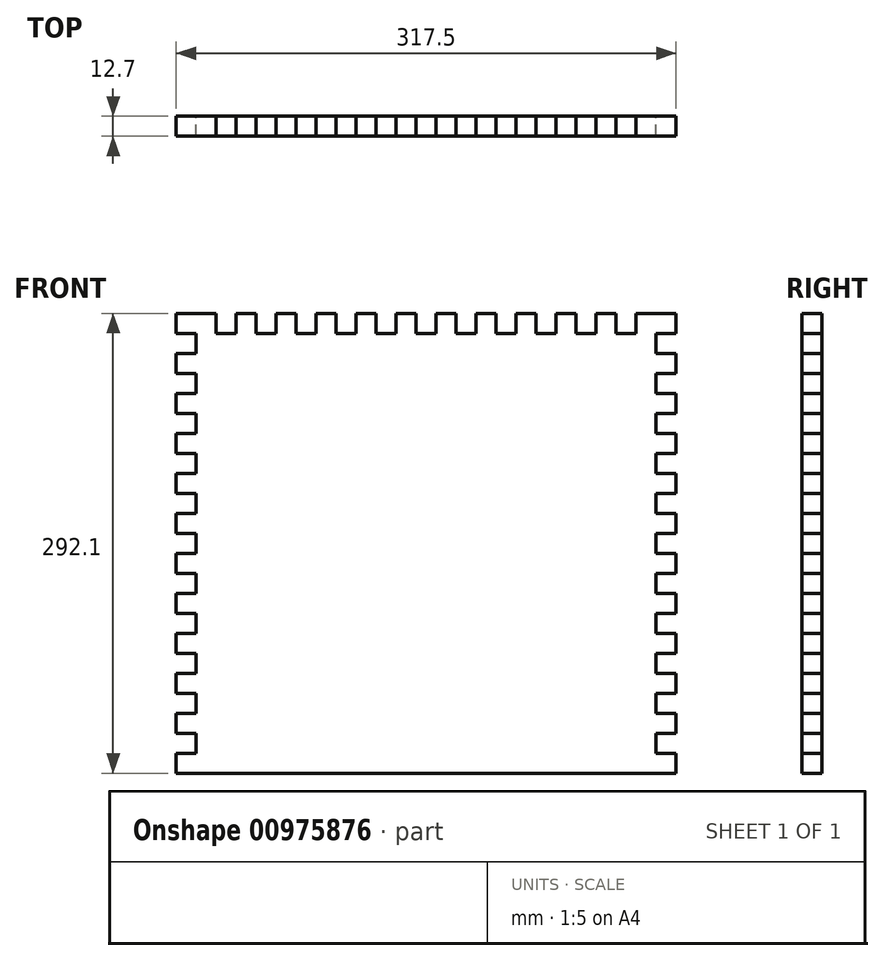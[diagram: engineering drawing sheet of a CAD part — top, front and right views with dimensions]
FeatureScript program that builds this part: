
annotation { "Feature Type Name" : "Feature", "Feature Type Description" : "" }
export const myFeature = defineFeature(function(context is Context, id is Id, definition is map)
    precondition{}
    {
        {
            var Q0;
            Q0=qCreatedBy(makeId("Front.planeOp"),FACE);
            var sketch = newSketch(context, id + "F0", { "sketchPlane" : qUnion([Q0])});
            skLineSegment(sketch, "E0.bottom", {"start": v(-125, 189.2) * mm, "end": v(167.1, 189.2) * mm});
            skLineSegment(sketch, "E0.top", {"start": v(-125, -102.9) * mm, "end": v(167.1, -102.9) * mm});
            skLineSegment(sketch, "E0.left", {"start": v(-125, 189.2) * mm, "end": v(-125, -102.9) * mm});
            skLineSegment(sketch, "E0.right", {"start": v(167.1, 189.2) * mm, "end": v(167.1, -102.9) * mm});
            skLineSegment(sketch, "E1.bottom", {"start": v(-125, 189.2) * mm, "end": v(-137.7, 189.2) * mm});
            skLineSegment(sketch, "E1.top", {"start": v(-125, 176.5) * mm, "end": v(-137.7, 176.5) * mm});
            skLineSegment(sketch, "E1.left", {"start": v(-125, 189.2) * mm, "end": v(-125, 176.5) * mm});
            skLineSegment(sketch, "E1.right", {"start": v(-137.7, 189.2) * mm, "end": v(-137.7, 176.5) * mm});
            skLineSegment(sketch, "E2.bottom", {"start": v(167.1, 189.2) * mm, "end": v(179.8, 189.2) * mm});
            skLineSegment(sketch, "E2.top", {"start": v(167.1, 176.5) * mm, "end": v(179.8, 176.5) * mm});
            skLineSegment(sketch, "E2.left", {"start": v(167.1, 189.2) * mm, "end": v(167.1, 176.5) * mm});
            skLineSegment(sketch, "E2.right", {"start": v(179.8, 189.2) * mm, "end": v(179.8, 176.5) * mm});
            skLineSegment(sketch, "E3.direction2", {"start": v(167.1, 176.5) * mm, "end": v(167.1, 176.5) * mm});
            skLineSegment(sketch, "E4.bottom", {"start": v(-112.3, 189.2) * mm, "end": v(-99.6, 189.2) * mm});
            skLineSegment(sketch, "E4.top", {"start": v(-112.3, 176.5) * mm, "end": v(-99.6, 176.5) * mm});
            skLineSegment(sketch, "E4.left", {"start": v(-112.3, 189.2) * mm, "end": v(-112.3, 176.5) * mm});
            skLineSegment(sketch, "E4.right", {"start": v(-99.6, 189.2) * mm, "end": v(-99.6, 176.5) * mm});
            skLineSegment(sketch, "E5.1.0.0", {"start": v(-86.9, 189.2) * mm, "end": v(-74.2, 189.2) * mm});
            skLineSegment(sketch, "E5.1.0.1", {"start": v(-86.9, 176.5) * mm, "end": v(-74.2, 176.5) * mm});
            skLineSegment(sketch, "E5.1.0.2", {"start": v(-74.2, 189.2) * mm, "end": v(-74.2, 176.5) * mm});
            skLineSegment(sketch, "E5.1.0.3", {"start": v(-86.9, 189.2) * mm, "end": v(-86.9, 176.5) * mm});
            skLineSegment(sketch, "E5.2.0.0", {"start": v(-61.5, 189.2) * mm, "end": v(-48.8, 189.2) * mm});
            skLineSegment(sketch, "E5.2.0.1", {"start": v(-61.5, 176.5) * mm, "end": v(-48.8, 176.5) * mm});
            skLineSegment(sketch, "E5.2.0.2", {"start": v(-48.8, 189.2) * mm, "end": v(-48.8, 176.5) * mm});
            skLineSegment(sketch, "E5.2.0.3", {"start": v(-61.5, 189.2) * mm, "end": v(-61.5, 176.5) * mm});
            skLineSegment(sketch, "E5.3.0.0", {"start": v(-36.1, 189.2) * mm, "end": v(-23.4, 189.2) * mm});
            skLineSegment(sketch, "E5.3.0.1", {"start": v(-36.1, 176.5) * mm, "end": v(-23.4, 176.5) * mm});
            skLineSegment(sketch, "E5.3.0.2", {"start": v(-23.4, 189.2) * mm, "end": v(-23.4, 176.5) * mm});
            skLineSegment(sketch, "E5.3.0.3", {"start": v(-36.1, 189.2) * mm, "end": v(-36.1, 176.5) * mm});
            skLineSegment(sketch, "E5.4.0.0", {"start": v(-10.7, 189.2) * mm, "end": v(2, 189.2) * mm});
            skLineSegment(sketch, "E5.4.0.1", {"start": v(-10.7, 176.5) * mm, "end": v(2, 176.5) * mm});
            skLineSegment(sketch, "E5.4.0.2", {"start": v(2, 189.2) * mm, "end": v(2, 176.5) * mm});
            skLineSegment(sketch, "E5.4.0.3", {"start": v(-10.7, 189.2) * mm, "end": v(-10.7, 176.5) * mm});
            skLineSegment(sketch, "E5.5.0.0", {"start": v(14.7, 189.2) * mm, "end": v(27.4, 189.2) * mm});
            skLineSegment(sketch, "E5.5.0.1", {"start": v(14.7, 176.5) * mm, "end": v(27.4, 176.5) * mm});
            skLineSegment(sketch, "E5.5.0.2", {"start": v(27.4, 189.2) * mm, "end": v(27.4, 176.5) * mm});
            skLineSegment(sketch, "E5.5.0.3", {"start": v(14.7, 189.2) * mm, "end": v(14.7, 176.5) * mm});
            skLineSegment(sketch, "E5.6.0.0", {"start": v(40.1, 189.2) * mm, "end": v(52.8, 189.2) * mm});
            skLineSegment(sketch, "E5.6.0.1", {"start": v(40.1, 176.5) * mm, "end": v(52.8, 176.5) * mm});
            skLineSegment(sketch, "E5.6.0.2", {"start": v(52.8, 189.2) * mm, "end": v(52.8, 176.5) * mm});
            skLineSegment(sketch, "E5.6.0.3", {"start": v(40.1, 189.2) * mm, "end": v(40.1, 176.5) * mm});
            skLineSegment(sketch, "E5.7.0.0", {"start": v(65.5, 189.2) * mm, "end": v(78.2, 189.2) * mm});
            skLineSegment(sketch, "E5.7.0.1", {"start": v(65.5, 176.5) * mm, "end": v(78.2, 176.5) * mm});
            skLineSegment(sketch, "E5.7.0.2", {"start": v(78.2, 189.2) * mm, "end": v(78.2, 176.5) * mm});
            skLineSegment(sketch, "E5.7.0.3", {"start": v(65.5, 189.2) * mm, "end": v(65.5, 176.5) * mm});
            skLineSegment(sketch, "E5.8.0.0", {"start": v(90.9, 189.2) * mm, "end": v(103.6, 189.2) * mm});
            skLineSegment(sketch, "E5.8.0.1", {"start": v(90.9, 176.5) * mm, "end": v(103.6, 176.5) * mm});
            skLineSegment(sketch, "E5.8.0.2", {"start": v(103.6, 189.2) * mm, "end": v(103.6, 176.5) * mm});
            skLineSegment(sketch, "E5.8.0.3", {"start": v(90.9, 189.2) * mm, "end": v(90.9, 176.5) * mm});
            skLineSegment(sketch, "E5.direction1", {"start": v(-112.3, 176.5) * mm, "end": v(-86.9, 176.5) * mm, "construction": true});
            skLineSegment(sketch, "E6.0.9.0", {"start": v(116.3, 189.2) * mm, "end": v(129, 189.2) * mm});
            skLineSegment(sketch, "E6.3.9.0", {"start": v(116.3, 176.5) * mm, "end": v(129, 176.5) * mm});
            skLineSegment(sketch, "E6.6.9.0", {"start": v(129, 189.2) * mm, "end": v(129, 176.5) * mm});
            skLineSegment(sketch, "E6.9.9.0", {"start": v(116.3, 189.2) * mm, "end": v(116.3, 176.5) * mm});
            skLineSegment(sketch, "E7.0.10.0", {"start": v(141.7, 189.2) * mm, "end": v(154.4, 189.2) * mm});
            skLineSegment(sketch, "E7.3.10.0", {"start": v(141.7, 176.5) * mm, "end": v(154.4, 176.5) * mm});
            skLineSegment(sketch, "E7.6.10.0", {"start": v(154.4, 189.2) * mm, "end": v(154.4, 176.5) * mm});
            skLineSegment(sketch, "E7.9.10.0", {"start": v(141.7, 189.2) * mm, "end": v(141.7, 176.5) * mm});
            skLineSegment(sketch, "E8.0.1.0", {"start": v(167.1, 151.1) * mm, "end": v(179.8, 151.1) * mm});
            skLineSegment(sketch, "E8.0.1.1", {"start": v(179.8, 163.8) * mm, "end": v(179.8, 151.1) * mm});
            skLineSegment(sketch, "E8.0.1.2", {"start": v(167.1, 163.8) * mm, "end": v(167.1, 151.1) * mm});
            skLineSegment(sketch, "E8.0.1.3", {"start": v(167.1, 163.8) * mm, "end": v(179.8, 163.8) * mm});
            skLineSegment(sketch, "E8.0.1.4", {"start": v(167.1, 163.8) * mm, "end": v(167.1, 151.1) * mm});
            skLineSegment(sketch, "E8.0.1.5", {"start": v(167.1, 151.1) * mm, "end": v(179.8, 151.1) * mm});
            skLineSegment(sketch, "E8.0.1.6", {"start": v(179.8, 163.8) * mm, "end": v(179.8, 151.1) * mm});
            skLineSegment(sketch, "E8.0.1.7", {"start": v(167.1, 163.8) * mm, "end": v(179.8, 163.8) * mm});
            skLineSegment(sketch, "E8.0.1.8", {"start": v(167.1, 163.8) * mm, "end": v(167.1, 151.1) * mm});
            skLineSegment(sketch, "E8.0.1.9", {"start": v(167.1, 151.1) * mm, "end": v(179.8, 151.1) * mm});
            skLineSegment(sketch, "E8.0.1.10", {"start": v(179.8, 163.8) * mm, "end": v(179.8, 151.1) * mm});
            skLineSegment(sketch, "E8.0.1.11", {"start": v(167.1, 163.8) * mm, "end": v(179.8, 163.8) * mm});
            skLineSegment(sketch, "E8.0.1.12", {"start": v(167.1, 151.1) * mm, "end": v(179.8, 151.1) * mm});
            skLineSegment(sketch, "E8.0.1.13", {"start": v(179.8, 163.8) * mm, "end": v(179.8, 151.1) * mm});
            skLineSegment(sketch, "E8.0.1.14", {"start": v(167.1, 163.8) * mm, "end": v(179.8, 163.8) * mm});
            skLineSegment(sketch, "E8.0.1.15", {"start": v(167.1, 163.8) * mm, "end": v(167.1, 151.1) * mm});
            skLineSegment(sketch, "E8.0.1.16", {"start": v(179.8, 163.8) * mm, "end": v(179.8, 151.1) * mm});
            skLineSegment(sketch, "E8.0.1.17", {"start": v(167.1, 163.8) * mm, "end": v(167.1, 151.1) * mm});
            skLineSegment(sketch, "E8.0.1.18", {"start": v(167.1, 163.8) * mm, "end": v(179.8, 163.8) * mm});
            skLineSegment(sketch, "E8.0.1.19", {"start": v(167.1, 151.1) * mm, "end": v(179.8, 151.1) * mm});
            skLineSegment(sketch, "E8.0.1.20", {"start": v(167.1, 163.8) * mm, "end": v(179.8, 163.8) * mm});
            skLineSegment(sketch, "E8.0.1.21", {"start": v(167.1, 151.1) * mm, "end": v(179.8, 151.1) * mm});
            skLineSegment(sketch, "E8.0.1.22", {"start": v(167.1, 163.8) * mm, "end": v(167.1, 151.1) * mm});
            skLineSegment(sketch, "E8.0.1.23", {"start": v(179.8, 163.8) * mm, "end": v(179.8, 151.1) * mm});
            skLineSegment(sketch, "E8.0.1.24", {"start": v(167.1, 163.8) * mm, "end": v(179.8, 163.8) * mm});
            skLineSegment(sketch, "E8.0.1.25", {"start": v(167.1, 163.8) * mm, "end": v(167.1, 151.1) * mm});
            skLineSegment(sketch, "E8.0.1.26", {"start": v(167.1, 151.1) * mm, "end": v(179.8, 151.1) * mm});
            skLineSegment(sketch, "E8.0.1.27", {"start": v(179.8, 163.8) * mm, "end": v(179.8, 151.1) * mm});
            skLineSegment(sketch, "E8.0.1.28", {"start": v(167.1, 163.8) * mm, "end": v(167.1, 151.1) * mm});
            skLineSegment(sketch, "E8.0.1.29", {"start": v(179.8, 163.8) * mm, "end": v(179.8, 151.1) * mm});
            skLineSegment(sketch, "E8.0.1.30", {"start": v(167.1, 163.8) * mm, "end": v(179.8, 163.8) * mm});
            skLineSegment(sketch, "E8.0.1.31", {"start": v(167.1, 151.1) * mm, "end": v(179.8, 151.1) * mm});
            skLineSegment(sketch, "E8.0.1.32", {"start": v(167.1, 163.8) * mm, "end": v(167.1, 151.1) * mm});
            skLineSegment(sketch, "E8.0.1.33", {"start": v(167.1, 163.8) * mm, "end": v(179.8, 163.8) * mm});
            skLineSegment(sketch, "E8.0.1.34", {"start": v(167.1, 151.1) * mm, "end": v(179.8, 151.1) * mm});
            skLineSegment(sketch, "E8.0.1.35", {"start": v(179.8, 163.8) * mm, "end": v(179.8, 151.1) * mm});
            skLineSegment(sketch, "E8.0.1.36", {"start": v(167.1, 151.1) * mm, "end": v(179.8, 151.1) * mm});
            skLineSegment(sketch, "E8.0.1.37", {"start": v(179.8, 163.8) * mm, "end": v(179.8, 151.1) * mm});
            skLineSegment(sketch, "E8.0.1.38", {"start": v(167.1, 163.8) * mm, "end": v(167.1, 151.1) * mm});
            skLineSegment(sketch, "E8.0.1.39", {"start": v(167.1, 163.8) * mm, "end": v(179.8, 163.8) * mm});
            skLineSegment(sketch, "E8.0.1.40", {"start": v(167.1, 163.8) * mm, "end": v(167.1, 151.1) * mm});
            skLineSegment(sketch, "E8.0.1.41", {"start": v(167.1, 151.1) * mm, "end": v(179.8, 151.1) * mm});
            skLineSegment(sketch, "E8.0.1.42", {"start": v(167.1, 163.8) * mm, "end": v(179.8, 163.8) * mm});
            skLineSegment(sketch, "E8.0.1.43", {"start": v(179.8, 163.8) * mm, "end": v(179.8, 151.1) * mm});
            skLineSegment(sketch, "E8.0.1.44", {"start": v(167.1, 163.8) * mm, "end": v(167.1, 151.1) * mm});
            skLineSegment(sketch, "E8.0.1.45", {"start": v(167.1, 151.1) * mm, "end": v(179.8, 151.1) * mm});
            skLineSegment(sketch, "E8.0.1.46", {"start": v(167.1, 163.8) * mm, "end": v(179.8, 163.8) * mm});
            skLineSegment(sketch, "E8.0.1.47", {"start": v(179.8, 163.8) * mm, "end": v(179.8, 151.1) * mm});
            skLineSegment(sketch, "E8.0.2.0", {"start": v(167.1, 125.7) * mm, "end": v(179.8, 125.7) * mm});
            skLineSegment(sketch, "E8.0.2.1", {"start": v(179.8, 138.4) * mm, "end": v(179.8, 125.7) * mm});
            skLineSegment(sketch, "E8.0.2.2", {"start": v(167.1, 138.4) * mm, "end": v(167.1, 125.7) * mm});
            skLineSegment(sketch, "E8.0.2.3", {"start": v(167.1, 138.4) * mm, "end": v(179.8, 138.4) * mm});
            skLineSegment(sketch, "E8.0.2.4", {"start": v(167.1, 138.4) * mm, "end": v(167.1, 125.7) * mm});
            skLineSegment(sketch, "E8.0.2.5", {"start": v(167.1, 125.7) * mm, "end": v(179.8, 125.7) * mm});
            skLineSegment(sketch, "E8.0.2.6", {"start": v(179.8, 138.4) * mm, "end": v(179.8, 125.7) * mm});
            skLineSegment(sketch, "E8.0.2.7", {"start": v(167.1, 138.4) * mm, "end": v(179.8, 138.4) * mm});
            skLineSegment(sketch, "E8.0.2.8", {"start": v(167.1, 138.4) * mm, "end": v(167.1, 125.7) * mm});
            skLineSegment(sketch, "E8.0.2.9", {"start": v(167.1, 125.7) * mm, "end": v(179.8, 125.7) * mm});
            skLineSegment(sketch, "E8.0.2.10", {"start": v(179.8, 138.4) * mm, "end": v(179.8, 125.7) * mm});
            skLineSegment(sketch, "E8.0.2.11", {"start": v(167.1, 138.4) * mm, "end": v(179.8, 138.4) * mm});
            skLineSegment(sketch, "E8.0.2.12", {"start": v(167.1, 125.7) * mm, "end": v(179.8, 125.7) * mm});
            skLineSegment(sketch, "E8.0.2.13", {"start": v(179.8, 138.4) * mm, "end": v(179.8, 125.7) * mm});
            skLineSegment(sketch, "E8.0.2.14", {"start": v(167.1, 138.4) * mm, "end": v(179.8, 138.4) * mm});
            skLineSegment(sketch, "E8.0.2.15", {"start": v(167.1, 138.4) * mm, "end": v(167.1, 125.7) * mm});
            skLineSegment(sketch, "E8.0.2.16", {"start": v(179.8, 138.4) * mm, "end": v(179.8, 125.7) * mm});
            skLineSegment(sketch, "E8.0.2.17", {"start": v(167.1, 138.4) * mm, "end": v(167.1, 125.7) * mm});
            skLineSegment(sketch, "E8.0.2.18", {"start": v(167.1, 138.4) * mm, "end": v(179.8, 138.4) * mm});
            skLineSegment(sketch, "E8.0.2.19", {"start": v(167.1, 125.7) * mm, "end": v(179.8, 125.7) * mm});
            skLineSegment(sketch, "E8.0.2.20", {"start": v(167.1, 138.4) * mm, "end": v(179.8, 138.4) * mm});
            skLineSegment(sketch, "E8.0.2.21", {"start": v(167.1, 125.7) * mm, "end": v(179.8, 125.7) * mm});
            skLineSegment(sketch, "E8.0.2.22", {"start": v(167.1, 138.4) * mm, "end": v(167.1, 125.7) * mm});
            skLineSegment(sketch, "E8.0.2.23", {"start": v(179.8, 138.4) * mm, "end": v(179.8, 125.7) * mm});
            skLineSegment(sketch, "E8.0.2.24", {"start": v(167.1, 138.4) * mm, "end": v(179.8, 138.4) * mm});
            skLineSegment(sketch, "E8.0.2.25", {"start": v(167.1, 138.4) * mm, "end": v(167.1, 125.7) * mm});
            skLineSegment(sketch, "E8.0.2.26", {"start": v(167.1, 125.7) * mm, "end": v(179.8, 125.7) * mm});
            skLineSegment(sketch, "E8.0.2.27", {"start": v(179.8, 138.4) * mm, "end": v(179.8, 125.7) * mm});
            skLineSegment(sketch, "E8.0.2.28", {"start": v(167.1, 138.4) * mm, "end": v(167.1, 125.7) * mm});
            skLineSegment(sketch, "E8.0.2.29", {"start": v(179.8, 138.4) * mm, "end": v(179.8, 125.7) * mm});
            skLineSegment(sketch, "E8.0.2.30", {"start": v(167.1, 138.4) * mm, "end": v(179.8, 138.4) * mm});
            skLineSegment(sketch, "E8.0.2.31", {"start": v(167.1, 125.7) * mm, "end": v(179.8, 125.7) * mm});
            skLineSegment(sketch, "E8.0.2.32", {"start": v(167.1, 138.4) * mm, "end": v(167.1, 125.7) * mm});
            skLineSegment(sketch, "E8.0.2.33", {"start": v(167.1, 138.4) * mm, "end": v(179.8, 138.4) * mm});
            skLineSegment(sketch, "E8.0.2.34", {"start": v(167.1, 125.7) * mm, "end": v(179.8, 125.7) * mm});
            skLineSegment(sketch, "E8.0.2.35", {"start": v(179.8, 138.4) * mm, "end": v(179.8, 125.7) * mm});
            skLineSegment(sketch, "E8.0.2.36", {"start": v(167.1, 125.7) * mm, "end": v(179.8, 125.7) * mm});
            skLineSegment(sketch, "E8.0.2.37", {"start": v(179.8, 138.4) * mm, "end": v(179.8, 125.7) * mm});
            skLineSegment(sketch, "E8.0.2.38", {"start": v(167.1, 138.4) * mm, "end": v(167.1, 125.7) * mm});
            skLineSegment(sketch, "E8.0.2.39", {"start": v(167.1, 138.4) * mm, "end": v(179.8, 138.4) * mm});
            skLineSegment(sketch, "E8.0.2.40", {"start": v(167.1, 138.4) * mm, "end": v(167.1, 125.7) * mm});
            skLineSegment(sketch, "E8.0.2.41", {"start": v(167.1, 125.7) * mm, "end": v(179.8, 125.7) * mm});
            skLineSegment(sketch, "E8.0.2.42", {"start": v(167.1, 138.4) * mm, "end": v(179.8, 138.4) * mm});
            skLineSegment(sketch, "E8.0.2.43", {"start": v(179.8, 138.4) * mm, "end": v(179.8, 125.7) * mm});
            skLineSegment(sketch, "E8.0.2.44", {"start": v(167.1, 138.4) * mm, "end": v(167.1, 125.7) * mm});
            skLineSegment(sketch, "E8.0.2.45", {"start": v(167.1, 125.7) * mm, "end": v(179.8, 125.7) * mm});
            skLineSegment(sketch, "E8.0.2.46", {"start": v(167.1, 138.4) * mm, "end": v(179.8, 138.4) * mm});
            skLineSegment(sketch, "E8.0.2.47", {"start": v(179.8, 138.4) * mm, "end": v(179.8, 125.7) * mm});
            skLineSegment(sketch, "E8.0.3.0", {"start": v(167.1, 100.3) * mm, "end": v(179.8, 100.3) * mm});
            skLineSegment(sketch, "E8.0.3.1", {"start": v(179.8, 113) * mm, "end": v(179.8, 100.3) * mm});
            skLineSegment(sketch, "E8.0.3.2", {"start": v(167.1, 113) * mm, "end": v(167.1, 100.3) * mm});
            skLineSegment(sketch, "E8.0.3.3", {"start": v(167.1, 113) * mm, "end": v(179.8, 113) * mm});
            skLineSegment(sketch, "E8.0.3.4", {"start": v(167.1, 113) * mm, "end": v(167.1, 100.3) * mm});
            skLineSegment(sketch, "E8.0.3.5", {"start": v(167.1, 100.3) * mm, "end": v(179.8, 100.3) * mm});
            skLineSegment(sketch, "E8.0.3.6", {"start": v(179.8, 113) * mm, "end": v(179.8, 100.3) * mm});
            skLineSegment(sketch, "E8.0.3.7", {"start": v(167.1, 113) * mm, "end": v(179.8, 113) * mm});
            skLineSegment(sketch, "E8.0.3.8", {"start": v(167.1, 113) * mm, "end": v(167.1, 100.3) * mm});
            skLineSegment(sketch, "E8.0.3.9", {"start": v(167.1, 100.3) * mm, "end": v(179.8, 100.3) * mm});
            skLineSegment(sketch, "E8.0.3.10", {"start": v(179.8, 113) * mm, "end": v(179.8, 100.3) * mm});
            skLineSegment(sketch, "E8.0.3.11", {"start": v(167.1, 113) * mm, "end": v(179.8, 113) * mm});
            skLineSegment(sketch, "E8.0.3.12", {"start": v(167.1, 100.3) * mm, "end": v(179.8, 100.3) * mm});
            skLineSegment(sketch, "E8.0.3.13", {"start": v(179.8, 113) * mm, "end": v(179.8, 100.3) * mm});
            skLineSegment(sketch, "E8.0.3.14", {"start": v(167.1, 113) * mm, "end": v(179.8, 113) * mm});
            skLineSegment(sketch, "E8.0.3.15", {"start": v(167.1, 113) * mm, "end": v(167.1, 100.3) * mm});
            skLineSegment(sketch, "E8.0.3.16", {"start": v(179.8, 113) * mm, "end": v(179.8, 100.3) * mm});
            skLineSegment(sketch, "E8.0.3.17", {"start": v(167.1, 113) * mm, "end": v(167.1, 100.3) * mm});
            skLineSegment(sketch, "E8.0.3.18", {"start": v(167.1, 113) * mm, "end": v(179.8, 113) * mm});
            skLineSegment(sketch, "E8.0.3.19", {"start": v(167.1, 100.3) * mm, "end": v(179.8, 100.3) * mm});
            skLineSegment(sketch, "E8.0.3.20", {"start": v(167.1, 113) * mm, "end": v(179.8, 113) * mm});
            skLineSegment(sketch, "E8.0.3.21", {"start": v(167.1, 100.3) * mm, "end": v(179.8, 100.3) * mm});
            skLineSegment(sketch, "E8.0.3.22", {"start": v(167.1, 113) * mm, "end": v(167.1, 100.3) * mm});
            skLineSegment(sketch, "E8.0.3.23", {"start": v(179.8, 113) * mm, "end": v(179.8, 100.3) * mm});
            skLineSegment(sketch, "E8.0.3.24", {"start": v(167.1, 113) * mm, "end": v(179.8, 113) * mm});
            skLineSegment(sketch, "E8.0.3.25", {"start": v(167.1, 113) * mm, "end": v(167.1, 100.3) * mm});
            skLineSegment(sketch, "E8.0.3.26", {"start": v(167.1, 100.3) * mm, "end": v(179.8, 100.3) * mm});
            skLineSegment(sketch, "E8.0.3.27", {"start": v(179.8, 113) * mm, "end": v(179.8, 100.3) * mm});
            skLineSegment(sketch, "E8.0.3.28", {"start": v(167.1, 113) * mm, "end": v(167.1, 100.3) * mm});
            skLineSegment(sketch, "E8.0.3.29", {"start": v(179.8, 113) * mm, "end": v(179.8, 100.3) * mm});
            skLineSegment(sketch, "E8.0.3.30", {"start": v(167.1, 113) * mm, "end": v(179.8, 113) * mm});
            skLineSegment(sketch, "E8.0.3.31", {"start": v(167.1, 100.3) * mm, "end": v(179.8, 100.3) * mm});
            skLineSegment(sketch, "E8.0.3.32", {"start": v(167.1, 113) * mm, "end": v(167.1, 100.3) * mm});
            skLineSegment(sketch, "E8.0.3.33", {"start": v(167.1, 113) * mm, "end": v(179.8, 113) * mm});
            skLineSegment(sketch, "E8.0.3.34", {"start": v(167.1, 100.3) * mm, "end": v(179.8, 100.3) * mm});
            skLineSegment(sketch, "E8.0.3.35", {"start": v(179.8, 113) * mm, "end": v(179.8, 100.3) * mm});
            skLineSegment(sketch, "E8.0.3.36", {"start": v(167.1, 100.3) * mm, "end": v(179.8, 100.3) * mm});
            skLineSegment(sketch, "E8.0.3.37", {"start": v(179.8, 113) * mm, "end": v(179.8, 100.3) * mm});
            skLineSegment(sketch, "E8.0.3.38", {"start": v(167.1, 113) * mm, "end": v(167.1, 100.3) * mm});
            skLineSegment(sketch, "E8.0.3.39", {"start": v(167.1, 113) * mm, "end": v(179.8, 113) * mm});
            skLineSegment(sketch, "E8.0.3.40", {"start": v(167.1, 113) * mm, "end": v(167.1, 100.3) * mm});
            skLineSegment(sketch, "E8.0.3.41", {"start": v(167.1, 100.3) * mm, "end": v(179.8, 100.3) * mm});
            skLineSegment(sketch, "E8.0.3.42", {"start": v(167.1, 113) * mm, "end": v(179.8, 113) * mm});
            skLineSegment(sketch, "E8.0.3.43", {"start": v(179.8, 113) * mm, "end": v(179.8, 100.3) * mm});
            skLineSegment(sketch, "E8.0.3.44", {"start": v(167.1, 113) * mm, "end": v(167.1, 100.3) * mm});
            skLineSegment(sketch, "E8.0.3.45", {"start": v(167.1, 100.3) * mm, "end": v(179.8, 100.3) * mm});
            skLineSegment(sketch, "E8.0.3.46", {"start": v(167.1, 113) * mm, "end": v(179.8, 113) * mm});
            skLineSegment(sketch, "E8.0.3.47", {"start": v(179.8, 113) * mm, "end": v(179.8, 100.3) * mm});
            skLineSegment(sketch, "E8.0.4.0", {"start": v(167.1, 74.9) * mm, "end": v(179.8, 74.9) * mm});
            skLineSegment(sketch, "E8.0.4.1", {"start": v(179.8, 87.6) * mm, "end": v(179.8, 74.9) * mm});
            skLineSegment(sketch, "E8.0.4.2", {"start": v(167.1, 87.6) * mm, "end": v(167.1, 74.9) * mm});
            skLineSegment(sketch, "E8.0.4.3", {"start": v(167.1, 87.6) * mm, "end": v(179.8, 87.6) * mm});
            skLineSegment(sketch, "E8.0.4.4", {"start": v(167.1, 87.6) * mm, "end": v(167.1, 74.9) * mm});
            skLineSegment(sketch, "E8.0.4.5", {"start": v(167.1, 74.9) * mm, "end": v(179.8, 74.9) * mm});
            skLineSegment(sketch, "E8.0.4.6", {"start": v(179.8, 87.6) * mm, "end": v(179.8, 74.9) * mm});
            skLineSegment(sketch, "E8.0.4.7", {"start": v(167.1, 87.6) * mm, "end": v(179.8, 87.6) * mm});
            skLineSegment(sketch, "E8.0.4.8", {"start": v(167.1, 87.6) * mm, "end": v(167.1, 74.9) * mm});
            skLineSegment(sketch, "E8.0.4.9", {"start": v(167.1, 74.9) * mm, "end": v(179.8, 74.9) * mm});
            skLineSegment(sketch, "E8.0.4.10", {"start": v(179.8, 87.6) * mm, "end": v(179.8, 74.9) * mm});
            skLineSegment(sketch, "E8.0.4.11", {"start": v(167.1, 87.6) * mm, "end": v(179.8, 87.6) * mm});
            skLineSegment(sketch, "E8.0.4.12", {"start": v(167.1, 74.9) * mm, "end": v(179.8, 74.9) * mm});
            skLineSegment(sketch, "E8.0.4.13", {"start": v(179.8, 87.6) * mm, "end": v(179.8, 74.9) * mm});
            skLineSegment(sketch, "E8.0.4.14", {"start": v(167.1, 87.6) * mm, "end": v(179.8, 87.6) * mm});
            skLineSegment(sketch, "E8.0.4.15", {"start": v(167.1, 87.6) * mm, "end": v(167.1, 74.9) * mm});
            skLineSegment(sketch, "E8.0.4.16", {"start": v(179.8, 87.6) * mm, "end": v(179.8, 74.9) * mm});
            skLineSegment(sketch, "E8.0.4.17", {"start": v(167.1, 87.6) * mm, "end": v(167.1, 74.9) * mm});
            skLineSegment(sketch, "E8.0.4.18", {"start": v(167.1, 87.6) * mm, "end": v(179.8, 87.6) * mm});
            skLineSegment(sketch, "E8.0.4.19", {"start": v(167.1, 74.9) * mm, "end": v(179.8, 74.9) * mm});
            skLineSegment(sketch, "E8.0.4.20", {"start": v(167.1, 87.6) * mm, "end": v(179.8, 87.6) * mm});
            skLineSegment(sketch, "E8.0.4.21", {"start": v(167.1, 74.9) * mm, "end": v(179.8, 74.9) * mm});
            skLineSegment(sketch, "E8.0.4.22", {"start": v(167.1, 87.6) * mm, "end": v(167.1, 74.9) * mm});
            skLineSegment(sketch, "E8.0.4.23", {"start": v(179.8, 87.6) * mm, "end": v(179.8, 74.9) * mm});
            skLineSegment(sketch, "E8.0.4.24", {"start": v(167.1, 87.6) * mm, "end": v(179.8, 87.6) * mm});
            skLineSegment(sketch, "E8.0.4.25", {"start": v(167.1, 87.6) * mm, "end": v(167.1, 74.9) * mm});
            skLineSegment(sketch, "E8.0.4.26", {"start": v(167.1, 74.9) * mm, "end": v(179.8, 74.9) * mm});
            skLineSegment(sketch, "E8.0.4.27", {"start": v(179.8, 87.6) * mm, "end": v(179.8, 74.9) * mm});
            skLineSegment(sketch, "E8.0.4.28", {"start": v(167.1, 87.6) * mm, "end": v(167.1, 74.9) * mm});
            skLineSegment(sketch, "E8.0.4.29", {"start": v(179.8, 87.6) * mm, "end": v(179.8, 74.9) * mm});
            skLineSegment(sketch, "E8.0.4.30", {"start": v(167.1, 87.6) * mm, "end": v(179.8, 87.6) * mm});
            skLineSegment(sketch, "E8.0.4.31", {"start": v(167.1, 74.9) * mm, "end": v(179.8, 74.9) * mm});
            skLineSegment(sketch, "E8.0.4.32", {"start": v(167.1, 87.6) * mm, "end": v(167.1, 74.9) * mm});
            skLineSegment(sketch, "E8.0.4.33", {"start": v(167.1, 87.6) * mm, "end": v(179.8, 87.6) * mm});
            skLineSegment(sketch, "E8.0.4.34", {"start": v(167.1, 74.9) * mm, "end": v(179.8, 74.9) * mm});
            skLineSegment(sketch, "E8.0.4.35", {"start": v(179.8, 87.6) * mm, "end": v(179.8, 74.9) * mm});
            skLineSegment(sketch, "E8.0.4.36", {"start": v(167.1, 74.9) * mm, "end": v(179.8, 74.9) * mm});
            skLineSegment(sketch, "E8.0.4.37", {"start": v(179.8, 87.6) * mm, "end": v(179.8, 74.9) * mm});
            skLineSegment(sketch, "E8.0.4.38", {"start": v(167.1, 87.6) * mm, "end": v(167.1, 74.9) * mm});
            skLineSegment(sketch, "E8.0.4.39", {"start": v(167.1, 87.6) * mm, "end": v(179.8, 87.6) * mm});
            skLineSegment(sketch, "E8.0.4.40", {"start": v(167.1, 87.6) * mm, "end": v(167.1, 74.9) * mm});
            skLineSegment(sketch, "E8.0.4.41", {"start": v(167.1, 74.9) * mm, "end": v(179.8, 74.9) * mm});
            skLineSegment(sketch, "E8.0.4.42", {"start": v(167.1, 87.6) * mm, "end": v(179.8, 87.6) * mm});
            skLineSegment(sketch, "E8.0.4.43", {"start": v(179.8, 87.6) * mm, "end": v(179.8, 74.9) * mm});
            skLineSegment(sketch, "E8.0.4.44", {"start": v(167.1, 87.6) * mm, "end": v(167.1, 74.9) * mm});
            skLineSegment(sketch, "E8.0.4.45", {"start": v(167.1, 74.9) * mm, "end": v(179.8, 74.9) * mm});
            skLineSegment(sketch, "E8.0.4.46", {"start": v(167.1, 87.6) * mm, "end": v(179.8, 87.6) * mm});
            skLineSegment(sketch, "E8.0.4.47", {"start": v(179.8, 87.6) * mm, "end": v(179.8, 74.9) * mm});
            skLineSegment(sketch, "E8.0.5.0", {"start": v(167.1, 49.5) * mm, "end": v(179.8, 49.5) * mm});
            skLineSegment(sketch, "E8.0.5.1", {"start": v(179.8, 62.2) * mm, "end": v(179.8, 49.5) * mm});
            skLineSegment(sketch, "E8.0.5.2", {"start": v(167.1, 62.2) * mm, "end": v(167.1, 49.5) * mm});
            skLineSegment(sketch, "E8.0.5.3", {"start": v(167.1, 62.2) * mm, "end": v(179.8, 62.2) * mm});
            skLineSegment(sketch, "E8.0.5.4", {"start": v(167.1, 62.2) * mm, "end": v(167.1, 49.5) * mm});
            skLineSegment(sketch, "E8.0.5.5", {"start": v(167.1, 49.5) * mm, "end": v(179.8, 49.5) * mm});
            skLineSegment(sketch, "E8.0.5.6", {"start": v(179.8, 62.2) * mm, "end": v(179.8, 49.5) * mm});
            skLineSegment(sketch, "E8.0.5.7", {"start": v(167.1, 62.2) * mm, "end": v(179.8, 62.2) * mm});
            skLineSegment(sketch, "E8.0.5.8", {"start": v(167.1, 62.2) * mm, "end": v(167.1, 49.5) * mm});
            skLineSegment(sketch, "E8.0.5.9", {"start": v(167.1, 49.5) * mm, "end": v(179.8, 49.5) * mm});
            skLineSegment(sketch, "E8.0.5.10", {"start": v(179.8, 62.2) * mm, "end": v(179.8, 49.5) * mm});
            skLineSegment(sketch, "E8.0.5.11", {"start": v(167.1, 62.2) * mm, "end": v(179.8, 62.2) * mm});
            skLineSegment(sketch, "E8.0.5.12", {"start": v(167.1, 49.5) * mm, "end": v(179.8, 49.5) * mm});
            skLineSegment(sketch, "E8.0.5.13", {"start": v(179.8, 62.2) * mm, "end": v(179.8, 49.5) * mm});
            skLineSegment(sketch, "E8.0.5.14", {"start": v(167.1, 62.2) * mm, "end": v(179.8, 62.2) * mm});
            skLineSegment(sketch, "E8.0.5.15", {"start": v(167.1, 62.2) * mm, "end": v(167.1, 49.5) * mm});
            skLineSegment(sketch, "E8.0.5.16", {"start": v(179.8, 62.2) * mm, "end": v(179.8, 49.5) * mm});
            skLineSegment(sketch, "E8.0.5.17", {"start": v(167.1, 62.2) * mm, "end": v(167.1, 49.5) * mm});
            skLineSegment(sketch, "E8.0.5.18", {"start": v(167.1, 62.2) * mm, "end": v(179.8, 62.2) * mm});
            skLineSegment(sketch, "E8.0.5.19", {"start": v(167.1, 49.5) * mm, "end": v(179.8, 49.5) * mm});
            skLineSegment(sketch, "E8.0.5.20", {"start": v(167.1, 62.2) * mm, "end": v(179.8, 62.2) * mm});
            skLineSegment(sketch, "E8.0.5.21", {"start": v(167.1, 49.5) * mm, "end": v(179.8, 49.5) * mm});
            skLineSegment(sketch, "E8.0.5.22", {"start": v(167.1, 62.2) * mm, "end": v(167.1, 49.5) * mm});
            skLineSegment(sketch, "E8.0.5.23", {"start": v(179.8, 62.2) * mm, "end": v(179.8, 49.5) * mm});
            skLineSegment(sketch, "E8.0.5.24", {"start": v(167.1, 62.2) * mm, "end": v(179.8, 62.2) * mm});
            skLineSegment(sketch, "E8.0.5.25", {"start": v(167.1, 62.2) * mm, "end": v(167.1, 49.5) * mm});
            skLineSegment(sketch, "E8.0.5.26", {"start": v(167.1, 49.5) * mm, "end": v(179.8, 49.5) * mm});
            skLineSegment(sketch, "E8.0.5.27", {"start": v(179.8, 62.2) * mm, "end": v(179.8, 49.5) * mm});
            skLineSegment(sketch, "E8.0.5.28", {"start": v(167.1, 62.2) * mm, "end": v(167.1, 49.5) * mm});
            skLineSegment(sketch, "E8.0.5.29", {"start": v(179.8, 62.2) * mm, "end": v(179.8, 49.5) * mm});
            skLineSegment(sketch, "E8.0.5.30", {"start": v(167.1, 62.2) * mm, "end": v(179.8, 62.2) * mm});
            skLineSegment(sketch, "E8.0.5.31", {"start": v(167.1, 49.5) * mm, "end": v(179.8, 49.5) * mm});
            skLineSegment(sketch, "E8.0.5.32", {"start": v(167.1, 62.2) * mm, "end": v(167.1, 49.5) * mm});
            skLineSegment(sketch, "E8.0.5.33", {"start": v(167.1, 62.2) * mm, "end": v(179.8, 62.2) * mm});
            skLineSegment(sketch, "E8.0.5.34", {"start": v(167.1, 49.5) * mm, "end": v(179.8, 49.5) * mm});
            skLineSegment(sketch, "E8.0.5.35", {"start": v(179.8, 62.2) * mm, "end": v(179.8, 49.5) * mm});
            skLineSegment(sketch, "E8.0.5.36", {"start": v(167.1, 49.5) * mm, "end": v(179.8, 49.5) * mm});
            skLineSegment(sketch, "E8.0.5.37", {"start": v(179.8, 62.2) * mm, "end": v(179.8, 49.5) * mm});
            skLineSegment(sketch, "E8.0.5.38", {"start": v(167.1, 62.2) * mm, "end": v(167.1, 49.5) * mm});
            skLineSegment(sketch, "E8.0.5.39", {"start": v(167.1, 62.2) * mm, "end": v(179.8, 62.2) * mm});
            skLineSegment(sketch, "E8.0.5.40", {"start": v(167.1, 62.2) * mm, "end": v(167.1, 49.5) * mm});
            skLineSegment(sketch, "E8.0.5.41", {"start": v(167.1, 49.5) * mm, "end": v(179.8, 49.5) * mm});
            skLineSegment(sketch, "E8.0.5.42", {"start": v(167.1, 62.2) * mm, "end": v(179.8, 62.2) * mm});
            skLineSegment(sketch, "E8.0.5.43", {"start": v(179.8, 62.2) * mm, "end": v(179.8, 49.5) * mm});
            skLineSegment(sketch, "E8.0.5.44", {"start": v(167.1, 62.2) * mm, "end": v(167.1, 49.5) * mm});
            skLineSegment(sketch, "E8.0.5.45", {"start": v(167.1, 49.5) * mm, "end": v(179.8, 49.5) * mm});
            skLineSegment(sketch, "E8.0.5.46", {"start": v(167.1, 62.2) * mm, "end": v(179.8, 62.2) * mm});
            skLineSegment(sketch, "E8.0.5.47", {"start": v(179.8, 62.2) * mm, "end": v(179.8, 49.5) * mm});
            skLineSegment(sketch, "E8.0.6.0", {"start": v(167.1, 24.1) * mm, "end": v(179.8, 24.1) * mm});
            skLineSegment(sketch, "E8.0.6.1", {"start": v(179.8, 36.8) * mm, "end": v(179.8, 24.1) * mm});
            skLineSegment(sketch, "E8.0.6.2", {"start": v(167.1, 36.8) * mm, "end": v(167.1, 24.1) * mm});
            skLineSegment(sketch, "E8.0.6.3", {"start": v(167.1, 36.8) * mm, "end": v(179.8, 36.8) * mm});
            skLineSegment(sketch, "E8.0.6.4", {"start": v(167.1, 36.8) * mm, "end": v(167.1, 24.1) * mm});
            skLineSegment(sketch, "E8.0.6.5", {"start": v(167.1, 24.1) * mm, "end": v(179.8, 24.1) * mm});
            skLineSegment(sketch, "E8.0.6.6", {"start": v(179.8, 36.8) * mm, "end": v(179.8, 24.1) * mm});
            skLineSegment(sketch, "E8.0.6.7", {"start": v(167.1, 36.8) * mm, "end": v(179.8, 36.8) * mm});
            skLineSegment(sketch, "E8.0.6.8", {"start": v(167.1, 36.8) * mm, "end": v(167.1, 24.1) * mm});
            skLineSegment(sketch, "E8.0.6.9", {"start": v(167.1, 24.1) * mm, "end": v(179.8, 24.1) * mm});
            skLineSegment(sketch, "E8.0.6.10", {"start": v(179.8, 36.8) * mm, "end": v(179.8, 24.1) * mm});
            skLineSegment(sketch, "E8.0.6.11", {"start": v(167.1, 36.8) * mm, "end": v(179.8, 36.8) * mm});
            skLineSegment(sketch, "E8.0.6.12", {"start": v(167.1, 24.1) * mm, "end": v(179.8, 24.1) * mm});
            skLineSegment(sketch, "E8.0.6.13", {"start": v(179.8, 36.8) * mm, "end": v(179.8, 24.1) * mm});
            skLineSegment(sketch, "E8.0.6.14", {"start": v(167.1, 36.8) * mm, "end": v(179.8, 36.8) * mm});
            skLineSegment(sketch, "E8.0.6.15", {"start": v(167.1, 36.8) * mm, "end": v(167.1, 24.1) * mm});
            skLineSegment(sketch, "E8.0.6.16", {"start": v(179.8, 36.8) * mm, "end": v(179.8, 24.1) * mm});
            skLineSegment(sketch, "E8.0.6.17", {"start": v(167.1, 36.8) * mm, "end": v(167.1, 24.1) * mm});
            skLineSegment(sketch, "E8.0.6.18", {"start": v(167.1, 36.8) * mm, "end": v(179.8, 36.8) * mm});
            skLineSegment(sketch, "E8.0.6.19", {"start": v(167.1, 24.1) * mm, "end": v(179.8, 24.1) * mm});
            skLineSegment(sketch, "E8.0.6.20", {"start": v(167.1, 36.8) * mm, "end": v(179.8, 36.8) * mm});
            skLineSegment(sketch, "E8.0.6.21", {"start": v(167.1, 24.1) * mm, "end": v(179.8, 24.1) * mm});
            skLineSegment(sketch, "E8.0.6.22", {"start": v(167.1, 36.8) * mm, "end": v(167.1, 24.1) * mm});
            skLineSegment(sketch, "E8.0.6.23", {"start": v(179.8, 36.8) * mm, "end": v(179.8, 24.1) * mm});
            skLineSegment(sketch, "E8.0.6.24", {"start": v(167.1, 36.8) * mm, "end": v(179.8, 36.8) * mm});
            skLineSegment(sketch, "E8.0.6.25", {"start": v(167.1, 36.8) * mm, "end": v(167.1, 24.1) * mm});
            skLineSegment(sketch, "E8.0.6.26", {"start": v(167.1, 24.1) * mm, "end": v(179.8, 24.1) * mm});
            skLineSegment(sketch, "E8.0.6.27", {"start": v(179.8, 36.8) * mm, "end": v(179.8, 24.1) * mm});
            skLineSegment(sketch, "E8.0.6.28", {"start": v(167.1, 36.8) * mm, "end": v(167.1, 24.1) * mm});
            skLineSegment(sketch, "E8.0.6.29", {"start": v(179.8, 36.8) * mm, "end": v(179.8, 24.1) * mm});
            skLineSegment(sketch, "E8.0.6.30", {"start": v(167.1, 36.8) * mm, "end": v(179.8, 36.8) * mm});
            skLineSegment(sketch, "E8.0.6.31", {"start": v(167.1, 24.1) * mm, "end": v(179.8, 24.1) * mm});
            skLineSegment(sketch, "E8.0.6.32", {"start": v(167.1, 36.8) * mm, "end": v(167.1, 24.1) * mm});
            skLineSegment(sketch, "E8.0.6.33", {"start": v(167.1, 36.8) * mm, "end": v(179.8, 36.8) * mm});
            skLineSegment(sketch, "E8.0.6.34", {"start": v(167.1, 24.1) * mm, "end": v(179.8, 24.1) * mm});
            skLineSegment(sketch, "E8.0.6.35", {"start": v(179.8, 36.8) * mm, "end": v(179.8, 24.1) * mm});
            skLineSegment(sketch, "E8.0.6.36", {"start": v(167.1, 24.1) * mm, "end": v(179.8, 24.1) * mm});
            skLineSegment(sketch, "E8.0.6.37", {"start": v(179.8, 36.8) * mm, "end": v(179.8, 24.1) * mm});
            skLineSegment(sketch, "E8.0.6.38", {"start": v(167.1, 36.8) * mm, "end": v(167.1, 24.1) * mm});
            skLineSegment(sketch, "E8.0.6.39", {"start": v(167.1, 36.8) * mm, "end": v(179.8, 36.8) * mm});
            skLineSegment(sketch, "E8.0.6.40", {"start": v(167.1, 36.8) * mm, "end": v(167.1, 24.1) * mm});
            skLineSegment(sketch, "E8.0.6.41", {"start": v(167.1, 24.1) * mm, "end": v(179.8, 24.1) * mm});
            skLineSegment(sketch, "E8.0.6.42", {"start": v(167.1, 36.8) * mm, "end": v(179.8, 36.8) * mm});
            skLineSegment(sketch, "E8.0.6.43", {"start": v(179.8, 36.8) * mm, "end": v(179.8, 24.1) * mm});
            skLineSegment(sketch, "E8.0.6.44", {"start": v(167.1, 36.8) * mm, "end": v(167.1, 24.1) * mm});
            skLineSegment(sketch, "E8.0.6.45", {"start": v(167.1, 24.1) * mm, "end": v(179.8, 24.1) * mm});
            skLineSegment(sketch, "E8.0.6.46", {"start": v(167.1, 36.8) * mm, "end": v(179.8, 36.8) * mm});
            skLineSegment(sketch, "E8.0.6.47", {"start": v(179.8, 36.8) * mm, "end": v(179.8, 24.1) * mm});
            skLineSegment(sketch, "E8.0.7.0", {"start": v(167.1, -1.3) * mm, "end": v(179.8, -1.3) * mm});
            skLineSegment(sketch, "E8.0.7.1", {"start": v(179.8, 11.4) * mm, "end": v(179.8, -1.3) * mm});
            skLineSegment(sketch, "E8.0.7.2", {"start": v(167.1, 11.4) * mm, "end": v(167.1, -1.3) * mm});
            skLineSegment(sketch, "E8.0.7.3", {"start": v(167.1, 11.4) * mm, "end": v(179.8, 11.4) * mm});
            skLineSegment(sketch, "E8.0.7.4", {"start": v(167.1, 11.4) * mm, "end": v(167.1, -1.3) * mm});
            skLineSegment(sketch, "E8.0.7.5", {"start": v(167.1, -1.3) * mm, "end": v(179.8, -1.3) * mm});
            skLineSegment(sketch, "E8.0.7.6", {"start": v(179.8, 11.4) * mm, "end": v(179.8, -1.3) * mm});
            skLineSegment(sketch, "E8.0.7.7", {"start": v(167.1, 11.4) * mm, "end": v(179.8, 11.4) * mm});
            skLineSegment(sketch, "E8.0.7.8", {"start": v(167.1, 11.4) * mm, "end": v(167.1, -1.3) * mm});
            skLineSegment(sketch, "E8.0.7.9", {"start": v(167.1, -1.3) * mm, "end": v(179.8, -1.3) * mm});
            skLineSegment(sketch, "E8.0.7.10", {"start": v(179.8, 11.4) * mm, "end": v(179.8, -1.3) * mm});
            skLineSegment(sketch, "E8.0.7.11", {"start": v(167.1, 11.4) * mm, "end": v(179.8, 11.4) * mm});
            skLineSegment(sketch, "E8.0.7.12", {"start": v(167.1, -1.3) * mm, "end": v(179.8, -1.3) * mm});
            skLineSegment(sketch, "E8.0.7.13", {"start": v(179.8, 11.4) * mm, "end": v(179.8, -1.3) * mm});
            skLineSegment(sketch, "E8.0.7.14", {"start": v(167.1, 11.4) * mm, "end": v(179.8, 11.4) * mm});
            skLineSegment(sketch, "E8.0.7.15", {"start": v(167.1, 11.4) * mm, "end": v(167.1, -1.3) * mm});
            skLineSegment(sketch, "E8.0.7.16", {"start": v(179.8, 11.4) * mm, "end": v(179.8, -1.3) * mm});
            skLineSegment(sketch, "E8.0.7.17", {"start": v(167.1, 11.4) * mm, "end": v(167.1, -1.3) * mm});
            skLineSegment(sketch, "E8.0.7.18", {"start": v(167.1, 11.4) * mm, "end": v(179.8, 11.4) * mm});
            skLineSegment(sketch, "E8.0.7.19", {"start": v(167.1, -1.3) * mm, "end": v(179.8, -1.3) * mm});
            skLineSegment(sketch, "E8.0.7.20", {"start": v(167.1, 11.4) * mm, "end": v(179.8, 11.4) * mm});
            skLineSegment(sketch, "E8.0.7.21", {"start": v(167.1, -1.3) * mm, "end": v(179.8, -1.3) * mm});
            skLineSegment(sketch, "E8.0.7.22", {"start": v(167.1, 11.4) * mm, "end": v(167.1, -1.3) * mm});
            skLineSegment(sketch, "E8.0.7.23", {"start": v(179.8, 11.4) * mm, "end": v(179.8, -1.3) * mm});
            skLineSegment(sketch, "E8.0.7.24", {"start": v(167.1, 11.4) * mm, "end": v(179.8, 11.4) * mm});
            skLineSegment(sketch, "E8.0.7.25", {"start": v(167.1, 11.4) * mm, "end": v(167.1, -1.3) * mm});
            skLineSegment(sketch, "E8.0.7.26", {"start": v(167.1, -1.3) * mm, "end": v(179.8, -1.3) * mm});
            skLineSegment(sketch, "E8.0.7.27", {"start": v(179.8, 11.4) * mm, "end": v(179.8, -1.3) * mm});
            skLineSegment(sketch, "E8.0.7.28", {"start": v(167.1, 11.4) * mm, "end": v(167.1, -1.3) * mm});
            skLineSegment(sketch, "E8.0.7.29", {"start": v(179.8, 11.4) * mm, "end": v(179.8, -1.3) * mm});
            skLineSegment(sketch, "E8.0.7.30", {"start": v(167.1, 11.4) * mm, "end": v(179.8, 11.4) * mm});
            skLineSegment(sketch, "E8.0.7.31", {"start": v(167.1, -1.3) * mm, "end": v(179.8, -1.3) * mm});
            skLineSegment(sketch, "E8.0.7.32", {"start": v(167.1, 11.4) * mm, "end": v(167.1, -1.3) * mm});
            skLineSegment(sketch, "E8.0.7.33", {"start": v(167.1, 11.4) * mm, "end": v(179.8, 11.4) * mm});
            skLineSegment(sketch, "E8.0.7.34", {"start": v(167.1, -1.3) * mm, "end": v(179.8, -1.3) * mm});
            skLineSegment(sketch, "E8.0.7.35", {"start": v(179.8, 11.4) * mm, "end": v(179.8, -1.3) * mm});
            skLineSegment(sketch, "E8.0.7.36", {"start": v(167.1, -1.3) * mm, "end": v(179.8, -1.3) * mm});
            skLineSegment(sketch, "E8.0.7.37", {"start": v(179.8, 11.4) * mm, "end": v(179.8, -1.3) * mm});
            skLineSegment(sketch, "E8.0.7.38", {"start": v(167.1, 11.4) * mm, "end": v(167.1, -1.3) * mm});
            skLineSegment(sketch, "E8.0.7.39", {"start": v(167.1, 11.4) * mm, "end": v(179.8, 11.4) * mm});
            skLineSegment(sketch, "E8.0.7.40", {"start": v(167.1, 11.4) * mm, "end": v(167.1, -1.3) * mm});
            skLineSegment(sketch, "E8.0.7.41", {"start": v(167.1, -1.3) * mm, "end": v(179.8, -1.3) * mm});
            skLineSegment(sketch, "E8.0.7.42", {"start": v(167.1, 11.4) * mm, "end": v(179.8, 11.4) * mm});
            skLineSegment(sketch, "E8.0.7.43", {"start": v(179.8, 11.4) * mm, "end": v(179.8, -1.3) * mm});
            skLineSegment(sketch, "E8.0.7.44", {"start": v(167.1, 11.4) * mm, "end": v(167.1, -1.3) * mm});
            skLineSegment(sketch, "E8.0.7.45", {"start": v(167.1, -1.3) * mm, "end": v(179.8, -1.3) * mm});
            skLineSegment(sketch, "E8.0.7.46", {"start": v(167.1, 11.4) * mm, "end": v(179.8, 11.4) * mm});
            skLineSegment(sketch, "E8.0.7.47", {"start": v(179.8, 11.4) * mm, "end": v(179.8, -1.3) * mm});
            skLineSegment(sketch, "E8.0.8.0", {"start": v(167.1, -26.7) * mm, "end": v(179.8, -26.7) * mm});
            skLineSegment(sketch, "E8.0.8.1", {"start": v(179.8, -14) * mm, "end": v(179.8, -26.7) * mm});
            skLineSegment(sketch, "E8.0.8.2", {"start": v(167.1, -14) * mm, "end": v(167.1, -26.7) * mm});
            skLineSegment(sketch, "E8.0.8.3", {"start": v(167.1, -14) * mm, "end": v(179.8, -14) * mm});
            skLineSegment(sketch, "E8.0.8.4", {"start": v(167.1, -14) * mm, "end": v(167.1, -26.7) * mm});
            skLineSegment(sketch, "E8.0.8.5", {"start": v(167.1, -26.7) * mm, "end": v(179.8, -26.7) * mm});
            skLineSegment(sketch, "E8.0.8.6", {"start": v(179.8, -14) * mm, "end": v(179.8, -26.7) * mm});
            skLineSegment(sketch, "E8.0.8.7", {"start": v(167.1, -14) * mm, "end": v(179.8, -14) * mm});
            skLineSegment(sketch, "E8.0.8.8", {"start": v(167.1, -14) * mm, "end": v(167.1, -26.7) * mm});
            skLineSegment(sketch, "E8.0.8.9", {"start": v(167.1, -26.7) * mm, "end": v(179.8, -26.7) * mm});
            skLineSegment(sketch, "E8.0.8.10", {"start": v(179.8, -14) * mm, "end": v(179.8, -26.7) * mm});
            skLineSegment(sketch, "E8.0.8.11", {"start": v(167.1, -14) * mm, "end": v(179.8, -14) * mm});
            skLineSegment(sketch, "E8.0.8.12", {"start": v(167.1, -26.7) * mm, "end": v(179.8, -26.7) * mm});
            skLineSegment(sketch, "E8.0.8.13", {"start": v(179.8, -14) * mm, "end": v(179.8, -26.7) * mm});
            skLineSegment(sketch, "E8.0.8.14", {"start": v(167.1, -14) * mm, "end": v(179.8, -14) * mm});
            skLineSegment(sketch, "E8.0.8.15", {"start": v(167.1, -14) * mm, "end": v(167.1, -26.7) * mm});
            skLineSegment(sketch, "E8.0.8.16", {"start": v(179.8, -14) * mm, "end": v(179.8, -26.7) * mm});
            skLineSegment(sketch, "E8.0.8.17", {"start": v(167.1, -14) * mm, "end": v(167.1, -26.7) * mm});
            skLineSegment(sketch, "E8.0.8.18", {"start": v(167.1, -14) * mm, "end": v(179.8, -14) * mm});
            skLineSegment(sketch, "E8.0.8.19", {"start": v(167.1, -26.7) * mm, "end": v(179.8, -26.7) * mm});
            skLineSegment(sketch, "E8.0.8.20", {"start": v(167.1, -14) * mm, "end": v(179.8, -14) * mm});
            skLineSegment(sketch, "E8.0.8.21", {"start": v(167.1, -26.7) * mm, "end": v(179.8, -26.7) * mm});
            skLineSegment(sketch, "E8.0.8.22", {"start": v(167.1, -14) * mm, "end": v(167.1, -26.7) * mm});
            skLineSegment(sketch, "E8.0.8.23", {"start": v(179.8, -14) * mm, "end": v(179.8, -26.7) * mm});
            skLineSegment(sketch, "E8.0.8.24", {"start": v(167.1, -14) * mm, "end": v(179.8, -14) * mm});
            skLineSegment(sketch, "E8.0.8.25", {"start": v(167.1, -14) * mm, "end": v(167.1, -26.7) * mm});
            skLineSegment(sketch, "E8.0.8.26", {"start": v(167.1, -26.7) * mm, "end": v(179.8, -26.7) * mm});
            skLineSegment(sketch, "E8.0.8.27", {"start": v(179.8, -14) * mm, "end": v(179.8, -26.7) * mm});
            skLineSegment(sketch, "E8.0.8.28", {"start": v(167.1, -14) * mm, "end": v(167.1, -26.7) * mm});
            skLineSegment(sketch, "E8.0.8.29", {"start": v(179.8, -14) * mm, "end": v(179.8, -26.7) * mm});
            skLineSegment(sketch, "E8.0.8.30", {"start": v(167.1, -14) * mm, "end": v(179.8, -14) * mm});
            skLineSegment(sketch, "E8.0.8.31", {"start": v(167.1, -26.7) * mm, "end": v(179.8, -26.7) * mm});
            skLineSegment(sketch, "E8.0.8.32", {"start": v(167.1, -14) * mm, "end": v(167.1, -26.7) * mm});
            skLineSegment(sketch, "E8.0.8.33", {"start": v(167.1, -14) * mm, "end": v(179.8, -14) * mm});
            skLineSegment(sketch, "E8.0.8.34", {"start": v(167.1, -26.7) * mm, "end": v(179.8, -26.7) * mm});
            skLineSegment(sketch, "E8.0.8.35", {"start": v(179.8, -14) * mm, "end": v(179.8, -26.7) * mm});
            skLineSegment(sketch, "E8.0.8.36", {"start": v(167.1, -26.7) * mm, "end": v(179.8, -26.7) * mm});
            skLineSegment(sketch, "E8.0.8.37", {"start": v(179.8, -14) * mm, "end": v(179.8, -26.7) * mm});
            skLineSegment(sketch, "E8.0.8.38", {"start": v(167.1, -14) * mm, "end": v(167.1, -26.7) * mm});
            skLineSegment(sketch, "E8.0.8.39", {"start": v(167.1, -14) * mm, "end": v(179.8, -14) * mm});
            skLineSegment(sketch, "E8.0.8.40", {"start": v(167.1, -14) * mm, "end": v(167.1, -26.7) * mm});
            skLineSegment(sketch, "E8.0.8.41", {"start": v(167.1, -26.7) * mm, "end": v(179.8, -26.7) * mm});
            skLineSegment(sketch, "E8.0.8.42", {"start": v(167.1, -14) * mm, "end": v(179.8, -14) * mm});
            skLineSegment(sketch, "E8.0.8.43", {"start": v(179.8, -14) * mm, "end": v(179.8, -26.7) * mm});
            skLineSegment(sketch, "E8.0.8.44", {"start": v(167.1, -14) * mm, "end": v(167.1, -26.7) * mm});
            skLineSegment(sketch, "E8.0.8.45", {"start": v(167.1, -26.7) * mm, "end": v(179.8, -26.7) * mm});
            skLineSegment(sketch, "E8.0.8.46", {"start": v(167.1, -14) * mm, "end": v(179.8, -14) * mm});
            skLineSegment(sketch, "E8.0.8.47", {"start": v(179.8, -14) * mm, "end": v(179.8, -26.7) * mm});
            skLineSegment(sketch, "E8.0.9.0", {"start": v(167.1, -52.1) * mm, "end": v(179.8, -52.1) * mm});
            skLineSegment(sketch, "E8.0.9.1", {"start": v(179.8, -39.4) * mm, "end": v(179.8, -52.1) * mm});
            skLineSegment(sketch, "E8.0.9.2", {"start": v(167.1, -39.4) * mm, "end": v(167.1, -52.1) * mm});
            skLineSegment(sketch, "E8.0.9.3", {"start": v(167.1, -39.4) * mm, "end": v(179.8, -39.4) * mm});
            skLineSegment(sketch, "E8.0.9.4", {"start": v(167.1, -39.4) * mm, "end": v(167.1, -52.1) * mm});
            skLineSegment(sketch, "E8.0.9.5", {"start": v(167.1, -52.1) * mm, "end": v(179.8, -52.1) * mm});
            skLineSegment(sketch, "E8.0.9.6", {"start": v(179.8, -39.4) * mm, "end": v(179.8, -52.1) * mm});
            skLineSegment(sketch, "E8.0.9.7", {"start": v(167.1, -39.4) * mm, "end": v(179.8, -39.4) * mm});
            skLineSegment(sketch, "E8.0.9.8", {"start": v(167.1, -39.4) * mm, "end": v(167.1, -52.1) * mm});
            skLineSegment(sketch, "E8.0.9.9", {"start": v(167.1, -52.1) * mm, "end": v(179.8, -52.1) * mm});
            skLineSegment(sketch, "E8.0.9.10", {"start": v(179.8, -39.4) * mm, "end": v(179.8, -52.1) * mm});
            skLineSegment(sketch, "E8.0.9.11", {"start": v(167.1, -39.4) * mm, "end": v(179.8, -39.4) * mm});
            skLineSegment(sketch, "E8.0.9.12", {"start": v(167.1, -52.1) * mm, "end": v(179.8, -52.1) * mm});
            skLineSegment(sketch, "E8.0.9.13", {"start": v(179.8, -39.4) * mm, "end": v(179.8, -52.1) * mm});
            skLineSegment(sketch, "E8.0.9.14", {"start": v(167.1, -39.4) * mm, "end": v(179.8, -39.4) * mm});
            skLineSegment(sketch, "E8.0.9.15", {"start": v(167.1, -39.4) * mm, "end": v(167.1, -52.1) * mm});
            skLineSegment(sketch, "E8.0.9.16", {"start": v(179.8, -39.4) * mm, "end": v(179.8, -52.1) * mm});
            skLineSegment(sketch, "E8.0.9.17", {"start": v(167.1, -39.4) * mm, "end": v(167.1, -52.1) * mm});
            skLineSegment(sketch, "E8.0.9.18", {"start": v(167.1, -39.4) * mm, "end": v(179.8, -39.4) * mm});
            skLineSegment(sketch, "E8.0.9.19", {"start": v(167.1, -52.1) * mm, "end": v(179.8, -52.1) * mm});
            skLineSegment(sketch, "E8.0.9.20", {"start": v(167.1, -39.4) * mm, "end": v(179.8, -39.4) * mm});
            skLineSegment(sketch, "E8.0.9.21", {"start": v(167.1, -52.1) * mm, "end": v(179.8, -52.1) * mm});
            skLineSegment(sketch, "E8.0.9.22", {"start": v(167.1, -39.4) * mm, "end": v(167.1, -52.1) * mm});
            skLineSegment(sketch, "E8.0.9.23", {"start": v(179.8, -39.4) * mm, "end": v(179.8, -52.1) * mm});
            skLineSegment(sketch, "E8.0.9.24", {"start": v(167.1, -39.4) * mm, "end": v(179.8, -39.4) * mm});
            skLineSegment(sketch, "E8.0.9.25", {"start": v(167.1, -39.4) * mm, "end": v(167.1, -52.1) * mm});
            skLineSegment(sketch, "E8.0.9.26", {"start": v(167.1, -52.1) * mm, "end": v(179.8, -52.1) * mm});
            skLineSegment(sketch, "E8.0.9.27", {"start": v(179.8, -39.4) * mm, "end": v(179.8, -52.1) * mm});
            skLineSegment(sketch, "E8.0.9.28", {"start": v(167.1, -39.4) * mm, "end": v(167.1, -52.1) * mm});
            skLineSegment(sketch, "E8.0.9.29", {"start": v(179.8, -39.4) * mm, "end": v(179.8, -52.1) * mm});
            skLineSegment(sketch, "E8.0.9.30", {"start": v(167.1, -39.4) * mm, "end": v(179.8, -39.4) * mm});
            skLineSegment(sketch, "E8.0.9.31", {"start": v(167.1, -52.1) * mm, "end": v(179.8, -52.1) * mm});
            skLineSegment(sketch, "E8.0.9.32", {"start": v(167.1, -39.4) * mm, "end": v(167.1, -52.1) * mm});
            skLineSegment(sketch, "E8.0.9.33", {"start": v(167.1, -39.4) * mm, "end": v(179.8, -39.4) * mm});
            skLineSegment(sketch, "E8.0.9.34", {"start": v(167.1, -52.1) * mm, "end": v(179.8, -52.1) * mm});
            skLineSegment(sketch, "E8.0.9.35", {"start": v(179.8, -39.4) * mm, "end": v(179.8, -52.1) * mm});
            skLineSegment(sketch, "E8.0.9.36", {"start": v(167.1, -52.1) * mm, "end": v(179.8, -52.1) * mm});
            skLineSegment(sketch, "E8.0.9.37", {"start": v(179.8, -39.4) * mm, "end": v(179.8, -52.1) * mm});
            skLineSegment(sketch, "E8.0.9.38", {"start": v(167.1, -39.4) * mm, "end": v(167.1, -52.1) * mm});
            skLineSegment(sketch, "E8.0.9.39", {"start": v(167.1, -39.4) * mm, "end": v(179.8, -39.4) * mm});
            skLineSegment(sketch, "E8.0.9.40", {"start": v(167.1, -39.4) * mm, "end": v(167.1, -52.1) * mm});
            skLineSegment(sketch, "E8.0.9.41", {"start": v(167.1, -52.1) * mm, "end": v(179.8, -52.1) * mm});
            skLineSegment(sketch, "E8.0.9.42", {"start": v(167.1, -39.4) * mm, "end": v(179.8, -39.4) * mm});
            skLineSegment(sketch, "E8.0.9.43", {"start": v(179.8, -39.4) * mm, "end": v(179.8, -52.1) * mm});
            skLineSegment(sketch, "E8.0.9.44", {"start": v(167.1, -39.4) * mm, "end": v(167.1, -52.1) * mm});
            skLineSegment(sketch, "E8.0.9.45", {"start": v(167.1, -52.1) * mm, "end": v(179.8, -52.1) * mm});
            skLineSegment(sketch, "E8.0.9.46", {"start": v(167.1, -39.4) * mm, "end": v(179.8, -39.4) * mm});
            skLineSegment(sketch, "E8.0.9.47", {"start": v(179.8, -39.4) * mm, "end": v(179.8, -52.1) * mm});
            skLineSegment(sketch, "E8.0.10.0", {"start": v(167.1, -77.5) * mm, "end": v(179.8, -77.5) * mm});
            skLineSegment(sketch, "E8.0.10.1", {"start": v(179.8, -64.8) * mm, "end": v(179.8, -77.5) * mm});
            skLineSegment(sketch, "E8.0.10.2", {"start": v(167.1, -64.8) * mm, "end": v(167.1, -77.5) * mm});
            skLineSegment(sketch, "E8.0.10.3", {"start": v(167.1, -64.8) * mm, "end": v(179.8, -64.8) * mm});
            skLineSegment(sketch, "E8.0.10.4", {"start": v(167.1, -64.8) * mm, "end": v(167.1, -77.5) * mm});
            skLineSegment(sketch, "E8.0.10.5", {"start": v(167.1, -77.5) * mm, "end": v(179.8, -77.5) * mm});
            skLineSegment(sketch, "E8.0.10.6", {"start": v(179.8, -64.8) * mm, "end": v(179.8, -77.5) * mm});
            skLineSegment(sketch, "E8.0.10.7", {"start": v(167.1, -64.8) * mm, "end": v(179.8, -64.8) * mm});
            skLineSegment(sketch, "E8.0.10.8", {"start": v(167.1, -64.8) * mm, "end": v(167.1, -77.5) * mm});
            skLineSegment(sketch, "E8.0.10.9", {"start": v(167.1, -77.5) * mm, "end": v(179.8, -77.5) * mm});
            skLineSegment(sketch, "E8.0.10.10", {"start": v(179.8, -64.8) * mm, "end": v(179.8, -77.5) * mm});
            skLineSegment(sketch, "E8.0.10.11", {"start": v(167.1, -64.8) * mm, "end": v(179.8, -64.8) * mm});
            skLineSegment(sketch, "E8.0.10.12", {"start": v(167.1, -77.5) * mm, "end": v(179.8, -77.5) * mm});
            skLineSegment(sketch, "E8.0.10.13", {"start": v(179.8, -64.8) * mm, "end": v(179.8, -77.5) * mm});
            skLineSegment(sketch, "E8.0.10.14", {"start": v(167.1, -64.8) * mm, "end": v(179.8, -64.8) * mm});
            skLineSegment(sketch, "E8.0.10.15", {"start": v(167.1, -64.8) * mm, "end": v(167.1, -77.5) * mm});
            skLineSegment(sketch, "E8.0.10.16", {"start": v(179.8, -64.8) * mm, "end": v(179.8, -77.5) * mm});
            skLineSegment(sketch, "E8.0.10.17", {"start": v(167.1, -64.8) * mm, "end": v(167.1, -77.5) * mm});
            skLineSegment(sketch, "E8.0.10.18", {"start": v(167.1, -64.8) * mm, "end": v(179.8, -64.8) * mm});
            skLineSegment(sketch, "E8.0.10.19", {"start": v(167.1, -77.5) * mm, "end": v(179.8, -77.5) * mm});
            skLineSegment(sketch, "E8.0.10.20", {"start": v(167.1, -64.8) * mm, "end": v(179.8, -64.8) * mm});
            skLineSegment(sketch, "E8.0.10.21", {"start": v(167.1, -77.5) * mm, "end": v(179.8, -77.5) * mm});
            skLineSegment(sketch, "E8.0.10.22", {"start": v(167.1, -64.8) * mm, "end": v(167.1, -77.5) * mm});
            skLineSegment(sketch, "E8.0.10.23", {"start": v(179.8, -64.8) * mm, "end": v(179.8, -77.5) * mm});
            skLineSegment(sketch, "E8.0.10.24", {"start": v(167.1, -64.8) * mm, "end": v(179.8, -64.8) * mm});
            skLineSegment(sketch, "E8.0.10.25", {"start": v(167.1, -64.8) * mm, "end": v(167.1, -77.5) * mm});
            skLineSegment(sketch, "E8.0.10.26", {"start": v(167.1, -77.5) * mm, "end": v(179.8, -77.5) * mm});
            skLineSegment(sketch, "E8.0.10.27", {"start": v(179.8, -64.8) * mm, "end": v(179.8, -77.5) * mm});
            skLineSegment(sketch, "E8.0.10.28", {"start": v(167.1, -64.8) * mm, "end": v(167.1, -77.5) * mm});
            skLineSegment(sketch, "E8.0.10.29", {"start": v(179.8, -64.8) * mm, "end": v(179.8, -77.5) * mm});
            skLineSegment(sketch, "E8.0.10.30", {"start": v(167.1, -64.8) * mm, "end": v(179.8, -64.8) * mm});
            skLineSegment(sketch, "E8.0.10.31", {"start": v(167.1, -77.5) * mm, "end": v(179.8, -77.5) * mm});
            skLineSegment(sketch, "E8.0.10.32", {"start": v(167.1, -64.8) * mm, "end": v(167.1, -77.5) * mm});
            skLineSegment(sketch, "E8.0.10.33", {"start": v(167.1, -64.8) * mm, "end": v(179.8, -64.8) * mm});
            skLineSegment(sketch, "E8.0.10.34", {"start": v(167.1, -77.5) * mm, "end": v(179.8, -77.5) * mm});
            skLineSegment(sketch, "E8.0.10.35", {"start": v(179.8, -64.8) * mm, "end": v(179.8, -77.5) * mm});
            skLineSegment(sketch, "E8.0.10.36", {"start": v(167.1, -77.5) * mm, "end": v(179.8, -77.5) * mm});
            skLineSegment(sketch, "E8.0.10.37", {"start": v(179.8, -64.8) * mm, "end": v(179.8, -77.5) * mm});
            skLineSegment(sketch, "E8.0.10.38", {"start": v(167.1, -64.8) * mm, "end": v(167.1, -77.5) * mm});
            skLineSegment(sketch, "E8.0.10.39", {"start": v(167.1, -64.8) * mm, "end": v(179.8, -64.8) * mm});
            skLineSegment(sketch, "E8.0.10.40", {"start": v(167.1, -64.8) * mm, "end": v(167.1, -77.5) * mm});
            skLineSegment(sketch, "E8.0.10.41", {"start": v(167.1, -77.5) * mm, "end": v(179.8, -77.5) * mm});
            skLineSegment(sketch, "E8.0.10.42", {"start": v(167.1, -64.8) * mm, "end": v(179.8, -64.8) * mm});
            skLineSegment(sketch, "E8.0.10.43", {"start": v(179.8, -64.8) * mm, "end": v(179.8, -77.5) * mm});
            skLineSegment(sketch, "E8.0.10.44", {"start": v(167.1, -64.8) * mm, "end": v(167.1, -77.5) * mm});
            skLineSegment(sketch, "E8.0.10.45", {"start": v(167.1, -77.5) * mm, "end": v(179.8, -77.5) * mm});
            skLineSegment(sketch, "E8.0.10.46", {"start": v(167.1, -64.8) * mm, "end": v(179.8, -64.8) * mm});
            skLineSegment(sketch, "E8.0.10.47", {"start": v(179.8, -64.8) * mm, "end": v(179.8, -77.5) * mm});
            skLineSegment(sketch, "E8.direction1", {"start": v(167.1, 176.5) * mm, "end": v(192.5, 176.5) * mm, "construction": true});
            skLineSegment(sketch, "E8.direction2", {"start": v(167.1, 176.5) * mm, "end": v(167.1, 151.1) * mm, "construction": true});
            skLineSegment(sketch, "E9.0.1.0", {"start": v(-137.7, 163.8) * mm, "end": v(-137.7, 151.1) * mm});
            skLineSegment(sketch, "E9.0.1.1", {"start": v(-125, 163.8) * mm, "end": v(-137.7, 163.8) * mm});
            skLineSegment(sketch, "E9.0.1.2", {"start": v(-125, 163.8) * mm, "end": v(-125, 151.1) * mm});
            skLineSegment(sketch, "E9.0.1.3", {"start": v(-125, 151.1) * mm, "end": v(-137.7, 151.1) * mm});
            skLineSegment(sketch, "E9.0.1.4", {"start": v(-125, 151.1) * mm, "end": v(-137.7, 151.1) * mm});
            skLineSegment(sketch, "E9.0.2.0", {"start": v(-137.7, 138.4) * mm, "end": v(-137.7, 125.7) * mm});
            skLineSegment(sketch, "E9.0.2.1", {"start": v(-125, 138.4) * mm, "end": v(-137.7, 138.4) * mm});
            skLineSegment(sketch, "E9.0.2.2", {"start": v(-125, 138.4) * mm, "end": v(-125, 125.7) * mm});
            skLineSegment(sketch, "E9.0.2.3", {"start": v(-125, 125.7) * mm, "end": v(-137.7, 125.7) * mm});
            skLineSegment(sketch, "E9.0.2.4", {"start": v(-125, 125.7) * mm, "end": v(-137.7, 125.7) * mm});
            skLineSegment(sketch, "E9.0.3.0", {"start": v(-137.7, 113) * mm, "end": v(-137.7, 100.3) * mm});
            skLineSegment(sketch, "E9.0.3.1", {"start": v(-125, 113) * mm, "end": v(-137.7, 113) * mm});
            skLineSegment(sketch, "E9.0.3.2", {"start": v(-125, 113) * mm, "end": v(-125, 100.3) * mm});
            skLineSegment(sketch, "E9.0.3.3", {"start": v(-125, 100.3) * mm, "end": v(-137.7, 100.3) * mm});
            skLineSegment(sketch, "E9.0.3.4", {"start": v(-125, 100.3) * mm, "end": v(-137.7, 100.3) * mm});
            skLineSegment(sketch, "E9.0.4.0", {"start": v(-137.7, 87.6) * mm, "end": v(-137.7, 74.9) * mm});
            skLineSegment(sketch, "E9.0.4.1", {"start": v(-125, 87.6) * mm, "end": v(-137.7, 87.6) * mm});
            skLineSegment(sketch, "E9.0.4.2", {"start": v(-125, 87.6) * mm, "end": v(-125, 74.9) * mm});
            skLineSegment(sketch, "E9.0.4.3", {"start": v(-125, 74.9) * mm, "end": v(-137.7, 74.9) * mm});
            skLineSegment(sketch, "E9.0.4.4", {"start": v(-125, 74.9) * mm, "end": v(-137.7, 74.9) * mm});
            skLineSegment(sketch, "E9.0.5.0", {"start": v(-137.7, 62.2) * mm, "end": v(-137.7, 49.5) * mm});
            skLineSegment(sketch, "E9.0.5.1", {"start": v(-125, 62.2) * mm, "end": v(-137.7, 62.2) * mm});
            skLineSegment(sketch, "E9.0.5.2", {"start": v(-125, 62.2) * mm, "end": v(-125, 49.5) * mm});
            skLineSegment(sketch, "E9.0.5.3", {"start": v(-125, 49.5) * mm, "end": v(-137.7, 49.5) * mm});
            skLineSegment(sketch, "E9.0.5.4", {"start": v(-125, 49.5) * mm, "end": v(-137.7, 49.5) * mm});
            skLineSegment(sketch, "E9.0.6.0", {"start": v(-137.7, 36.8) * mm, "end": v(-137.7, 24.1) * mm});
            skLineSegment(sketch, "E9.0.6.1", {"start": v(-125, 36.8) * mm, "end": v(-137.7, 36.8) * mm});
            skLineSegment(sketch, "E9.0.6.2", {"start": v(-125, 36.8) * mm, "end": v(-125, 24.1) * mm});
            skLineSegment(sketch, "E9.0.6.3", {"start": v(-125, 24.1) * mm, "end": v(-137.7, 24.1) * mm});
            skLineSegment(sketch, "E9.0.6.4", {"start": v(-125, 24.1) * mm, "end": v(-137.7, 24.1) * mm});
            skLineSegment(sketch, "E9.0.7.0", {"start": v(-137.7, 11.4) * mm, "end": v(-137.7, -1.3) * mm});
            skLineSegment(sketch, "E9.0.7.1", {"start": v(-125, 11.4) * mm, "end": v(-137.7, 11.4) * mm});
            skLineSegment(sketch, "E9.0.7.2", {"start": v(-125, 11.4) * mm, "end": v(-125, -1.3) * mm});
            skLineSegment(sketch, "E9.0.7.3", {"start": v(-125, -1.3) * mm, "end": v(-137.7, -1.3) * mm});
            skLineSegment(sketch, "E9.0.7.4", {"start": v(-125, -1.3) * mm, "end": v(-137.7, -1.3) * mm});
            skLineSegment(sketch, "E9.0.8.0", {"start": v(-137.7, -14) * mm, "end": v(-137.7, -26.7) * mm});
            skLineSegment(sketch, "E9.0.8.1", {"start": v(-125, -14) * mm, "end": v(-137.7, -14) * mm});
            skLineSegment(sketch, "E9.0.8.2", {"start": v(-125, -14) * mm, "end": v(-125, -26.7) * mm});
            skLineSegment(sketch, "E9.0.8.3", {"start": v(-125, -26.7) * mm, "end": v(-137.7, -26.7) * mm});
            skLineSegment(sketch, "E9.0.8.4", {"start": v(-125, -26.7) * mm, "end": v(-137.7, -26.7) * mm});
            skLineSegment(sketch, "E9.0.9.0", {"start": v(-137.7, -39.4) * mm, "end": v(-137.7, -52.1) * mm});
            skLineSegment(sketch, "E9.0.9.1", {"start": v(-125, -39.4) * mm, "end": v(-137.7, -39.4) * mm});
            skLineSegment(sketch, "E9.0.9.2", {"start": v(-125, -39.4) * mm, "end": v(-125, -52.1) * mm});
            skLineSegment(sketch, "E9.0.9.3", {"start": v(-125, -52.1) * mm, "end": v(-137.7, -52.1) * mm});
            skLineSegment(sketch, "E9.0.9.4", {"start": v(-125, -52.1) * mm, "end": v(-137.7, -52.1) * mm});
            skLineSegment(sketch, "E9.0.10.0", {"start": v(-137.7, -64.8) * mm, "end": v(-137.7, -77.5) * mm});
            skLineSegment(sketch, "E9.0.10.1", {"start": v(-125, -64.8) * mm, "end": v(-137.7, -64.8) * mm});
            skLineSegment(sketch, "E9.0.10.2", {"start": v(-125, -64.8) * mm, "end": v(-125, -77.5) * mm});
            skLineSegment(sketch, "E9.0.10.3", {"start": v(-125, -77.5) * mm, "end": v(-137.7, -77.5) * mm});
            skLineSegment(sketch, "E9.0.10.4", {"start": v(-125, -77.5) * mm, "end": v(-137.7, -77.5) * mm});
            skLineSegment(sketch, "E9.0.11.0", {"start": v(-137.7, -90.2) * mm, "end": v(-137.7, -102.9) * mm});
            skLineSegment(sketch, "E9.0.11.1", {"start": v(-125, -90.2) * mm, "end": v(-137.7, -90.2) * mm});
            skLineSegment(sketch, "E9.0.11.2", {"start": v(-125, -90.2) * mm, "end": v(-125, -102.9) * mm});
            skLineSegment(sketch, "E9.0.11.3", {"start": v(-125, -102.9) * mm, "end": v(-137.7, -102.9) * mm});
            skLineSegment(sketch, "E9.0.11.4", {"start": v(-125, -102.9) * mm, "end": v(-137.7, -102.9) * mm});
            skLineSegment(sketch, "E9.direction1", {"start": v(-137.7, 176.5) * mm, "end": v(-112.3, 176.5) * mm, "construction": true});
            skLineSegment(sketch, "E9.direction2", {"start": v(-137.7, 176.5) * mm, "end": v(-137.7, 151.1) * mm, "construction": true});
            skLineSegment(sketch, "E10.0.0.11", {"start": v(167.1, -102.9) * mm, "end": v(179.8, -102.9) * mm});
            skLineSegment(sketch, "E10.3.0.11", {"start": v(179.8, -90.2) * mm, "end": v(179.8, -102.9) * mm});
            skLineSegment(sketch, "E10.6.0.11", {"start": v(167.1, -90.2) * mm, "end": v(167.1, -102.9) * mm});
            skLineSegment(sketch, "E10.9.0.11", {"start": v(167.1, -90.2) * mm, "end": v(179.8, -90.2) * mm});
            skLineSegment(sketch, "E10.12.0.11", {"start": v(167.1, -90.2) * mm, "end": v(167.1, -102.9) * mm});
            skLineSegment(sketch, "E10.15.0.11", {"start": v(167.1, -102.9) * mm, "end": v(179.8, -102.9) * mm});
            skLineSegment(sketch, "E10.18.0.11", {"start": v(179.8, -90.2) * mm, "end": v(179.8, -102.9) * mm});
            skLineSegment(sketch, "E10.21.0.11", {"start": v(167.1, -90.2) * mm, "end": v(179.8, -90.2) * mm});
            skLineSegment(sketch, "E10.24.0.11", {"start": v(167.1, -90.2) * mm, "end": v(167.1, -102.9) * mm});
            skLineSegment(sketch, "E10.27.0.11", {"start": v(167.1, -102.9) * mm, "end": v(179.8, -102.9) * mm});
            skLineSegment(sketch, "E10.30.0.11", {"start": v(179.8, -90.2) * mm, "end": v(179.8, -102.9) * mm});
            skLineSegment(sketch, "E10.33.0.11", {"start": v(167.1, -90.2) * mm, "end": v(179.8, -90.2) * mm});
            skLineSegment(sketch, "E10.36.0.11", {"start": v(167.1, -102.9) * mm, "end": v(179.8, -102.9) * mm});
            skLineSegment(sketch, "E10.39.0.11", {"start": v(179.8, -90.2) * mm, "end": v(179.8, -102.9) * mm});
            skLineSegment(sketch, "E10.42.0.11", {"start": v(167.1, -90.2) * mm, "end": v(179.8, -90.2) * mm});
            skLineSegment(sketch, "E10.45.0.11", {"start": v(167.1, -90.2) * mm, "end": v(167.1, -102.9) * mm});
            skLineSegment(sketch, "E10.48.0.11", {"start": v(179.8, -90.2) * mm, "end": v(179.8, -102.9) * mm});
            skLineSegment(sketch, "E10.51.0.11", {"start": v(167.1, -90.2) * mm, "end": v(167.1, -102.9) * mm});
            skLineSegment(sketch, "E10.54.0.11", {"start": v(167.1, -90.2) * mm, "end": v(179.8, -90.2) * mm});
            skLineSegment(sketch, "E10.57.0.11", {"start": v(167.1, -102.9) * mm, "end": v(179.8, -102.9) * mm});
            skLineSegment(sketch, "E10.60.0.11", {"start": v(167.1, -90.2) * mm, "end": v(179.8, -90.2) * mm});
            skLineSegment(sketch, "E10.63.0.11", {"start": v(167.1, -102.9) * mm, "end": v(179.8, -102.9) * mm});
            skLineSegment(sketch, "E10.66.0.11", {"start": v(167.1, -90.2) * mm, "end": v(167.1, -102.9) * mm});
            skLineSegment(sketch, "E10.69.0.11", {"start": v(179.8, -90.2) * mm, "end": v(179.8, -102.9) * mm});
            skLineSegment(sketch, "E10.72.0.11", {"start": v(167.1, -90.2) * mm, "end": v(179.8, -90.2) * mm});
            skLineSegment(sketch, "E10.75.0.11", {"start": v(167.1, -90.2) * mm, "end": v(167.1, -102.9) * mm});
            skLineSegment(sketch, "E10.78.0.11", {"start": v(167.1, -102.9) * mm, "end": v(179.8, -102.9) * mm});
            skLineSegment(sketch, "E10.81.0.11", {"start": v(179.8, -90.2) * mm, "end": v(179.8, -102.9) * mm});
            skLineSegment(sketch, "E10.84.0.11", {"start": v(167.1, -90.2) * mm, "end": v(167.1, -102.9) * mm});
            skLineSegment(sketch, "E10.87.0.11", {"start": v(179.8, -90.2) * mm, "end": v(179.8, -102.9) * mm});
            skLineSegment(sketch, "E10.90.0.11", {"start": v(167.1, -90.2) * mm, "end": v(179.8, -90.2) * mm});
            skLineSegment(sketch, "E10.93.0.11", {"start": v(167.1, -102.9) * mm, "end": v(179.8, -102.9) * mm});
            skLineSegment(sketch, "E10.96.0.11", {"start": v(167.1, -90.2) * mm, "end": v(167.1, -102.9) * mm});
            skLineSegment(sketch, "E10.99.0.11", {"start": v(167.1, -90.2) * mm, "end": v(179.8, -90.2) * mm});
            skLineSegment(sketch, "E10.102.0.11", {"start": v(167.1, -102.9) * mm, "end": v(179.8, -102.9) * mm});
            skLineSegment(sketch, "E10.105.0.11", {"start": v(179.8, -90.2) * mm, "end": v(179.8, -102.9) * mm});
            skLineSegment(sketch, "E10.108.0.11", {"start": v(167.1, -102.9) * mm, "end": v(179.8, -102.9) * mm});
            skLineSegment(sketch, "E10.111.0.11", {"start": v(179.8, -90.2) * mm, "end": v(179.8, -102.9) * mm});
            skLineSegment(sketch, "E10.114.0.11", {"start": v(167.1, -90.2) * mm, "end": v(167.1, -102.9) * mm});
            skLineSegment(sketch, "E10.117.0.11", {"start": v(167.1, -90.2) * mm, "end": v(179.8, -90.2) * mm});
            skLineSegment(sketch, "E10.120.0.11", {"start": v(167.1, -90.2) * mm, "end": v(167.1, -102.9) * mm});
            skLineSegment(sketch, "E10.123.0.11", {"start": v(167.1, -102.9) * mm, "end": v(179.8, -102.9) * mm});
            skLineSegment(sketch, "E10.126.0.11", {"start": v(167.1, -90.2) * mm, "end": v(179.8, -90.2) * mm});
            skLineSegment(sketch, "E10.129.0.11", {"start": v(179.8, -90.2) * mm, "end": v(179.8, -102.9) * mm});
            skLineSegment(sketch, "E10.132.0.11", {"start": v(167.1, -90.2) * mm, "end": v(167.1, -102.9) * mm});
            skLineSegment(sketch, "E10.135.0.11", {"start": v(167.1, -102.9) * mm, "end": v(179.8, -102.9) * mm});
            skLineSegment(sketch, "E10.138.0.11", {"start": v(167.1, -90.2) * mm, "end": v(179.8, -90.2) * mm});
            skLineSegment(sketch, "E10.141.0.11", {"start": v(179.8, -90.2) * mm, "end": v(179.8, -102.9) * mm});
            skSolve(sketch);
        }
        {
            var Q0;
            {var subQ0=sQuery(id+"F0.wireOp",EDGE,"E1.bottom");Q0=makeQuery(id+"F0.imprint","IMPRINT",FACE,{"disambiguationData":[TD([[makeQuery(id+"F0.imprint","IMPRINT",EDGE,{"derivedFrom":subQ0}),1.0]])]});}
            var Q1;
            Q1=makeQuery(id+"F0.imprint","IMPRINT",FACE,{"disambiguationData":[TD([[makeQuery(id+"F0.imprint","IMPRINT",EDGE,{"derivedFrom":sQuery(id+"F0.wireOp",EDGE,"E9.0.1.0")}),1.0]])]});
            var Q2;
            {var subQ37=sQuery(id+"F0.wireOp",EDGE,"E0.top");Q2=makeQuery(id+"F0.imprint","IMPRINT",FACE,{"disambiguationData":[TD([[makeQuery(id+"F0.imprint","IMPRINT",EDGE,{"derivedFrom":subQ37}),1.0]])]});}
            var Q3;
            {var subQ0=sQuery(id+"F0.wireOp",EDGE,"E2.bottom");Q3=makeQuery(id+"F0.imprint","IMPRINT",FACE,{"disambiguationData":[TD([[makeQuery(id+"F0.imprint","IMPRINT",EDGE,{"derivedFrom":subQ0}),-1.0]])]});}
            var Q4;
            {var subQ0=sQuery(id+"F0.wireOp",EDGE,"E8.0.1.0");Q4=makeQuery(id+"F0.imprint","IMPRINT",FACE,{"disambiguationData":[TD([[makeQuery(id+"F0.imprint","IMPRINT",EDGE,{"derivedFrom":subQ0}),1.0]])]});}
            var Q5;
            {var subQ0=sQuery(id+"F0.wireOp",EDGE,"E8.0.2.0");Q5=makeQuery(id+"F0.imprint","IMPRINT",FACE,{"disambiguationData":[TD([[makeQuery(id+"F0.imprint","IMPRINT",EDGE,{"derivedFrom":subQ0}),1.0]])]});}
            var Q6;
            {var subQ0=sQuery(id+"F0.wireOp",EDGE,"E8.0.3.0");Q6=makeQuery(id+"F0.imprint","IMPRINT",FACE,{"disambiguationData":[TD([[makeQuery(id+"F0.imprint","IMPRINT",EDGE,{"derivedFrom":subQ0}),1.0]])]});}
            var Q7;
            {var subQ0=sQuery(id+"F0.wireOp",EDGE,"E8.0.4.0");Q7=makeQuery(id+"F0.imprint","IMPRINT",FACE,{"disambiguationData":[TD([[makeQuery(id+"F0.imprint","IMPRINT",EDGE,{"derivedFrom":subQ0}),1.0]])]});}
            var Q8;
            {var subQ0=sQuery(id+"F0.wireOp",EDGE,"E8.0.5.0");Q8=makeQuery(id+"F0.imprint","IMPRINT",FACE,{"disambiguationData":[TD([[makeQuery(id+"F0.imprint","IMPRINT",EDGE,{"derivedFrom":subQ0}),1.0]])]});}
            var Q9;
            {var subQ0=sQuery(id+"F0.wireOp",EDGE,"E8.0.6.0");Q9=makeQuery(id+"F0.imprint","IMPRINT",FACE,{"disambiguationData":[TD([[makeQuery(id+"F0.imprint","IMPRINT",EDGE,{"derivedFrom":subQ0}),1.0]])]});}
            var Q10;
            {var subQ0=sQuery(id+"F0.wireOp",EDGE,"E8.0.7.0");Q10=makeQuery(id+"F0.imprint","IMPRINT",FACE,{"disambiguationData":[TD([[makeQuery(id+"F0.imprint","IMPRINT",EDGE,{"derivedFrom":subQ0}),1.0]])]});}
            var Q11;
            {var subQ0=sQuery(id+"F0.wireOp",EDGE,"E8.0.8.0");Q11=makeQuery(id+"F0.imprint","IMPRINT",FACE,{"disambiguationData":[TD([[makeQuery(id+"F0.imprint","IMPRINT",EDGE,{"derivedFrom":subQ0}),1.0]])]});}
            var Q12;
            {var subQ0=sQuery(id+"F0.wireOp",EDGE,"E8.0.9.0");Q12=makeQuery(id+"F0.imprint","IMPRINT",FACE,{"disambiguationData":[TD([[makeQuery(id+"F0.imprint","IMPRINT",EDGE,{"derivedFrom":subQ0}),1.0]])]});}
            var Q13;
            {var subQ0=sQuery(id+"F0.wireOp",EDGE,"E8.0.10.0");Q13=makeQuery(id+"F0.imprint","IMPRINT",FACE,{"disambiguationData":[TD([[makeQuery(id+"F0.imprint","IMPRINT",EDGE,{"derivedFrom":subQ0}),1.0]])]});}
            var Q14;
            {var subQ0=sQuery(id+"F0.wireOp",EDGE,"E10.0.0.11");Q14=makeQuery(id+"F0.imprint","IMPRINT",FACE,{"disambiguationData":[TD([[makeQuery(id+"F0.imprint","IMPRINT",EDGE,{"derivedFrom":subQ0}),1.0]])]});}
            var Q15;
            Q15=makeQuery(id+"F0.imprint","IMPRINT",FACE,{"disambiguationData":[TD([[makeQuery(id+"F0.imprint","IMPRINT",EDGE,{"derivedFrom":sQuery(id+"F0.wireOp",EDGE,"E9.0.11.0")}),1.0]])]});
            var Q16;
            Q16=makeQuery(id+"F0.imprint","IMPRINT",FACE,{"disambiguationData":[TD([[makeQuery(id+"F0.imprint","IMPRINT",EDGE,{"derivedFrom":sQuery(id+"F0.wireOp",EDGE,"E9.0.10.0")}),1.0]])]});
            var Q17;
            Q17=makeQuery(id+"F0.imprint","IMPRINT",FACE,{"disambiguationData":[TD([[makeQuery(id+"F0.imprint","IMPRINT",EDGE,{"derivedFrom":sQuery(id+"F0.wireOp",EDGE,"E9.0.9.0")}),1.0]])]});
            var Q18;
            Q18=makeQuery(id+"F0.imprint","IMPRINT",FACE,{"disambiguationData":[TD([[makeQuery(id+"F0.imprint","IMPRINT",EDGE,{"derivedFrom":sQuery(id+"F0.wireOp",EDGE,"E9.0.8.0")}),1.0]])]});
            var Q19;
            Q19=makeQuery(id+"F0.imprint","IMPRINT",FACE,{"disambiguationData":[TD([[makeQuery(id+"F0.imprint","IMPRINT",EDGE,{"derivedFrom":sQuery(id+"F0.wireOp",EDGE,"E9.0.7.0")}),1.0]])]});
            var Q20;
            Q20=makeQuery(id+"F0.imprint","IMPRINT",FACE,{"disambiguationData":[TD([[makeQuery(id+"F0.imprint","IMPRINT",EDGE,{"derivedFrom":sQuery(id+"F0.wireOp",EDGE,"E9.0.6.0")}),1.0]])]});
            var Q21;
            Q21=makeQuery(id+"F0.imprint","IMPRINT",FACE,{"disambiguationData":[TD([[makeQuery(id+"F0.imprint","IMPRINT",EDGE,{"derivedFrom":sQuery(id+"F0.wireOp",EDGE,"E9.0.5.0")}),1.0]])]});
            var Q22;
            Q22=makeQuery(id+"F0.imprint","IMPRINT",FACE,{"disambiguationData":[TD([[makeQuery(id+"F0.imprint","IMPRINT",EDGE,{"derivedFrom":sQuery(id+"F0.wireOp",EDGE,"E9.0.4.0")}),1.0]])]});
            var Q23;
            Q23=makeQuery(id+"F0.imprint","IMPRINT",FACE,{"disambiguationData":[TD([[makeQuery(id+"F0.imprint","IMPRINT",EDGE,{"derivedFrom":sQuery(id+"F0.wireOp",EDGE,"E9.0.3.0")}),1.0]])]});
            var Q24;
            Q24=makeQuery(id+"F0.imprint","IMPRINT",FACE,{"disambiguationData":[TD([[makeQuery(id+"F0.imprint","IMPRINT",EDGE,{"derivedFrom":sQuery(id+"F0.wireOp",EDGE,"E9.0.2.0")}),1.0]])]});
            extrude(context, id + "F1", {"entities" : qUnion([Q0, Q1, Q2, Q3, Q4, Q5, Q6, Q7, Q8, Q9, Q10, Q11, Q12, Q13, Q14, Q15, Q16, Q17, Q18, Q19, Q20, Q21, Q22, Q23, Q24]), "depth" : 12.7 * mm, "offsetDistance" : 25.4 * mm});
        }
        {
            var Q0;
            Q0=makeQuery(id+"F1.opExtrude","SWEPT_BODY",BODY,{"disambiguationData":[OSD([sQuery(id+"F0.wireOp",EDGE,"E0.bottom"),sQuery(id+"F0.wireOp",EDGE,"E0.top"),sQuery(id+"F0.wireOp",EDGE,"E0.left"),sQuery(id+"F0.wireOp",EDGE,"E0.right"),sQuery(id+"F0.wireOp",EDGE,"E1.bottom"),sQuery(id+"F0.wireOp",EDGE,"E1.top"),sQuery(id+"F0.wireOp",EDGE,"E1.right"),sQuery(id+"F0.wireOp",EDGE,"E2.bottom"),sQuery(id+"F0.wireOp",EDGE,"E2.top"),sQuery(id+"F0.wireOp",EDGE,"E2.right"),sQuery(id+"F0.wireOp",EDGE,"E4.top"),sQuery(id+"F0.wireOp",EDGE,"E4.left"),sQuery(id+"F0.wireOp",EDGE,"E4.right"),sQuery(id+"F0.wireOp",EDGE,"E5.1.0.1"),sQuery(id+"F0.wireOp",EDGE,"E5.1.0.2"),sQuery(id+"F0.wireOp",EDGE,"E5.1.0.3"),sQuery(id+"F0.wireOp",EDGE,"E5.2.0.1"),sQuery(id+"F0.wireOp",EDGE,"E5.2.0.2"),sQuery(id+"F0.wireOp",EDGE,"E5.2.0.3"),sQuery(id+"F0.wireOp",EDGE,"E5.3.0.1"),sQuery(id+"F0.wireOp",EDGE,"E5.3.0.2"),sQuery(id+"F0.wireOp",EDGE,"E5.3.0.3"),sQuery(id+"F0.wireOp",EDGE,"E5.4.0.1"),sQuery(id+"F0.wireOp",EDGE,"E5.4.0.2"),sQuery(id+"F0.wireOp",EDGE,"E5.4.0.3"),sQuery(id+"F0.wireOp",EDGE,"E5.5.0.1"),sQuery(id+"F0.wireOp",EDGE,"E5.5.0.2"),sQuery(id+"F0.wireOp",EDGE,"E5.5.0.3"),sQuery(id+"F0.wireOp",EDGE,"E5.6.0.1"),sQuery(id+"F0.wireOp",EDGE,"E5.6.0.2"),sQuery(id+"F0.wireOp",EDGE,"E5.6.0.3"),sQuery(id+"F0.wireOp",EDGE,"E5.7.0.1"),sQuery(id+"F0.wireOp",EDGE,"E5.7.0.2"),sQuery(id+"F0.wireOp",EDGE,"E5.7.0.3"),sQuery(id+"F0.wireOp",EDGE,"E5.8.0.1"),sQuery(id+"F0.wireOp",EDGE,"E5.8.0.2"),sQuery(id+"F0.wireOp",EDGE,"E5.8.0.3"),sQuery(id+"F0.wireOp",EDGE,"E6.3.9.0"),sQuery(id+"F0.wireOp",EDGE,"E6.6.9.0"),sQuery(id+"F0.wireOp",EDGE,"E6.9.9.0"),sQuery(id+"F0.wireOp",EDGE,"E7.3.10.0"),sQuery(id+"F0.wireOp",EDGE,"E7.6.10.0"),sQuery(id+"F0.wireOp",EDGE,"E7.9.10.0"),sQuery(id+"F0.wireOp",EDGE,"E8.0.1.0"),sQuery(id+"F0.wireOp",EDGE,"E8.0.1.1"),sQuery(id+"F0.wireOp",EDGE,"E8.0.1.3"),sQuery(id+"F0.wireOp",EDGE,"E8.0.2.0"),sQuery(id+"F0.wireOp",EDGE,"E8.0.2.1"),sQuery(id+"F0.wireOp",EDGE,"E8.0.2.3"),sQuery(id+"F0.wireOp",EDGE,"E8.0.3.0"),sQuery(id+"F0.wireOp",EDGE,"E8.0.3.1"),sQuery(id+"F0.wireOp",EDGE,"E8.0.3.3"),sQuery(id+"F0.wireOp",EDGE,"E8.0.4.0"),sQuery(id+"F0.wireOp",EDGE,"E8.0.4.1"),sQuery(id+"F0.wireOp",EDGE,"E8.0.4.3"),sQuery(id+"F0.wireOp",EDGE,"E8.0.5.0"),sQuery(id+"F0.wireOp",EDGE,"E8.0.5.1"),sQuery(id+"F0.wireOp",EDGE,"E8.0.5.3"),sQuery(id+"F0.wireOp",EDGE,"E8.0.6.0"),sQuery(id+"F0.wireOp",EDGE,"E8.0.6.1"),sQuery(id+"F0.wireOp",EDGE,"E8.0.6.3"),sQuery(id+"F0.wireOp",EDGE,"E8.0.7.0"),sQuery(id+"F0.wireOp",EDGE,"E8.0.7.1"),sQuery(id+"F0.wireOp",EDGE,"E8.0.7.3"),sQuery(id+"F0.wireOp",EDGE,"E8.0.8.0"),sQuery(id+"F0.wireOp",EDGE,"E8.0.8.1"),sQuery(id+"F0.wireOp",EDGE,"E8.0.8.3"),sQuery(id+"F0.wireOp",EDGE,"E8.0.9.0"),sQuery(id+"F0.wireOp",EDGE,"E8.0.9.1"),sQuery(id+"F0.wireOp",EDGE,"E8.0.9.3"),sQuery(id+"F0.wireOp",EDGE,"E8.0.10.0"),sQuery(id+"F0.wireOp",EDGE,"E8.0.10.1"),sQuery(id+"F0.wireOp",EDGE,"E8.0.10.3"),sQuery(id+"F0.wireOp",EDGE,"E9.0.1.0"),sQuery(id+"F0.wireOp",EDGE,"E9.0.1.1"),sQuery(id+"F0.wireOp",EDGE,"E9.0.1.3"),sQuery(id+"F0.wireOp",EDGE,"E9.0.2.0"),sQuery(id+"F0.wireOp",EDGE,"E9.0.2.1"),sQuery(id+"F0.wireOp",EDGE,"E9.0.2.3"),sQuery(id+"F0.wireOp",EDGE,"E9.0.3.0"),sQuery(id+"F0.wireOp",EDGE,"E9.0.3.1"),sQuery(id+"F0.wireOp",EDGE,"E9.0.3.3"),sQuery(id+"F0.wireOp",EDGE,"E9.0.4.0"),sQuery(id+"F0.wireOp",EDGE,"E9.0.4.1"),sQuery(id+"F0.wireOp",EDGE,"E9.0.4.3"),sQuery(id+"F0.wireOp",EDGE,"E9.0.5.0"),sQuery(id+"F0.wireOp",EDGE,"E9.0.5.1"),sQuery(id+"F0.wireOp",EDGE,"E9.0.5.3"),sQuery(id+"F0.wireOp",EDGE,"E9.0.6.0"),sQuery(id+"F0.wireOp",EDGE,"E9.0.6.1"),sQuery(id+"F0.wireOp",EDGE,"E9.0.6.3"),sQuery(id+"F0.wireOp",EDGE,"E9.0.7.0"),sQuery(id+"F0.wireOp",EDGE,"E9.0.7.1"),sQuery(id+"F0.wireOp",EDGE,"E9.0.7.3"),sQuery(id+"F0.wireOp",EDGE,"E9.0.8.0"),sQuery(id+"F0.wireOp",EDGE,"E9.0.8.1"),sQuery(id+"F0.wireOp",EDGE,"E9.0.8.3"),sQuery(id+"F0.wireOp",EDGE,"E9.0.9.0"),sQuery(id+"F0.wireOp",EDGE,"E9.0.9.1"),sQuery(id+"F0.wireOp",EDGE,"E9.0.9.3"),sQuery(id+"F0.wireOp",EDGE,"E9.0.10.0"),sQuery(id+"F0.wireOp",EDGE,"E9.0.10.1"),sQuery(id+"F0.wireOp",EDGE,"E9.0.10.3"),sQuery(id+"F0.wireOp",EDGE,"E9.0.11.0"),sQuery(id+"F0.wireOp",EDGE,"E9.0.11.1"),sQuery(id+"F0.wireOp",EDGE,"E9.0.11.3"),sQuery(id+"F0.wireOp",EDGE,"E10.0.0.11"),sQuery(id+"F0.wireOp",EDGE,"E10.3.0.11"),sQuery(id+"F0.wireOp",EDGE,"E10.9.0.11")])]});
            transform(context, id + "F2", {"entities" : qUnion([Q0]), "transformType" : TransformType.TRANSLATION_3D, "dx" : 0 * mm, "dy" : 0 * mm, "dz" : 0 * mm, "makeCopy" : true});
        }
        {
            var Q0;
            Q0=makeQuery(id+"F1.opExtrude","SWEPT_BODY",BODY,{"disambiguationData":[OSD([sQuery(id+"F0.wireOp",EDGE,"E0.bottom"),sQuery(id+"F0.wireOp",EDGE,"E0.top"),sQuery(id+"F0.wireOp",EDGE,"E0.left"),sQuery(id+"F0.wireOp",EDGE,"E0.right"),sQuery(id+"F0.wireOp",EDGE,"E1.bottom"),sQuery(id+"F0.wireOp",EDGE,"E1.top"),sQuery(id+"F0.wireOp",EDGE,"E1.right"),sQuery(id+"F0.wireOp",EDGE,"E2.bottom"),sQuery(id+"F0.wireOp",EDGE,"E2.top"),sQuery(id+"F0.wireOp",EDGE,"E2.right"),sQuery(id+"F0.wireOp",EDGE,"E4.top"),sQuery(id+"F0.wireOp",EDGE,"E4.left"),sQuery(id+"F0.wireOp",EDGE,"E4.right"),sQuery(id+"F0.wireOp",EDGE,"E5.1.0.1"),sQuery(id+"F0.wireOp",EDGE,"E5.1.0.2"),sQuery(id+"F0.wireOp",EDGE,"E5.1.0.3"),sQuery(id+"F0.wireOp",EDGE,"E5.2.0.1"),sQuery(id+"F0.wireOp",EDGE,"E5.2.0.2"),sQuery(id+"F0.wireOp",EDGE,"E5.2.0.3"),sQuery(id+"F0.wireOp",EDGE,"E5.3.0.1"),sQuery(id+"F0.wireOp",EDGE,"E5.3.0.2"),sQuery(id+"F0.wireOp",EDGE,"E5.3.0.3"),sQuery(id+"F0.wireOp",EDGE,"E5.4.0.1"),sQuery(id+"F0.wireOp",EDGE,"E5.4.0.2"),sQuery(id+"F0.wireOp",EDGE,"E5.4.0.3"),sQuery(id+"F0.wireOp",EDGE,"E5.5.0.1"),sQuery(id+"F0.wireOp",EDGE,"E5.5.0.2"),sQuery(id+"F0.wireOp",EDGE,"E5.5.0.3"),sQuery(id+"F0.wireOp",EDGE,"E5.6.0.1"),sQuery(id+"F0.wireOp",EDGE,"E5.6.0.2"),sQuery(id+"F0.wireOp",EDGE,"E5.6.0.3"),sQuery(id+"F0.wireOp",EDGE,"E5.7.0.1"),sQuery(id+"F0.wireOp",EDGE,"E5.7.0.2"),sQuery(id+"F0.wireOp",EDGE,"E5.7.0.3"),sQuery(id+"F0.wireOp",EDGE,"E5.8.0.1"),sQuery(id+"F0.wireOp",EDGE,"E5.8.0.2"),sQuery(id+"F0.wireOp",EDGE,"E5.8.0.3"),sQuery(id+"F0.wireOp",EDGE,"E6.3.9.0"),sQuery(id+"F0.wireOp",EDGE,"E6.6.9.0"),sQuery(id+"F0.wireOp",EDGE,"E6.9.9.0"),sQuery(id+"F0.wireOp",EDGE,"E7.3.10.0"),sQuery(id+"F0.wireOp",EDGE,"E7.6.10.0"),sQuery(id+"F0.wireOp",EDGE,"E7.9.10.0"),sQuery(id+"F0.wireOp",EDGE,"E8.0.1.0"),sQuery(id+"F0.wireOp",EDGE,"E8.0.1.1"),sQuery(id+"F0.wireOp",EDGE,"E8.0.1.3"),sQuery(id+"F0.wireOp",EDGE,"E8.0.2.0"),sQuery(id+"F0.wireOp",EDGE,"E8.0.2.1"),sQuery(id+"F0.wireOp",EDGE,"E8.0.2.3"),sQuery(id+"F0.wireOp",EDGE,"E8.0.3.0"),sQuery(id+"F0.wireOp",EDGE,"E8.0.3.1"),sQuery(id+"F0.wireOp",EDGE,"E8.0.3.3"),sQuery(id+"F0.wireOp",EDGE,"E8.0.4.0"),sQuery(id+"F0.wireOp",EDGE,"E8.0.4.1"),sQuery(id+"F0.wireOp",EDGE,"E8.0.4.3"),sQuery(id+"F0.wireOp",EDGE,"E8.0.5.0"),sQuery(id+"F0.wireOp",EDGE,"E8.0.5.1"),sQuery(id+"F0.wireOp",EDGE,"E8.0.5.3"),sQuery(id+"F0.wireOp",EDGE,"E8.0.6.0"),sQuery(id+"F0.wireOp",EDGE,"E8.0.6.1"),sQuery(id+"F0.wireOp",EDGE,"E8.0.6.3"),sQuery(id+"F0.wireOp",EDGE,"E8.0.7.0"),sQuery(id+"F0.wireOp",EDGE,"E8.0.7.1"),sQuery(id+"F0.wireOp",EDGE,"E8.0.7.3"),sQuery(id+"F0.wireOp",EDGE,"E8.0.8.0"),sQuery(id+"F0.wireOp",EDGE,"E8.0.8.1"),sQuery(id+"F0.wireOp",EDGE,"E8.0.8.3"),sQuery(id+"F0.wireOp",EDGE,"E8.0.9.0"),sQuery(id+"F0.wireOp",EDGE,"E8.0.9.1"),sQuery(id+"F0.wireOp",EDGE,"E8.0.9.3"),sQuery(id+"F0.wireOp",EDGE,"E8.0.10.0"),sQuery(id+"F0.wireOp",EDGE,"E8.0.10.1"),sQuery(id+"F0.wireOp",EDGE,"E8.0.10.3"),sQuery(id+"F0.wireOp",EDGE,"E9.0.1.0"),sQuery(id+"F0.wireOp",EDGE,"E9.0.1.1"),sQuery(id+"F0.wireOp",EDGE,"E9.0.1.3"),sQuery(id+"F0.wireOp",EDGE,"E9.0.2.0"),sQuery(id+"F0.wireOp",EDGE,"E9.0.2.1"),sQuery(id+"F0.wireOp",EDGE,"E9.0.2.3"),sQuery(id+"F0.wireOp",EDGE,"E9.0.3.0"),sQuery(id+"F0.wireOp",EDGE,"E9.0.3.1"),sQuery(id+"F0.wireOp",EDGE,"E9.0.3.3"),sQuery(id+"F0.wireOp",EDGE,"E9.0.4.0"),sQuery(id+"F0.wireOp",EDGE,"E9.0.4.1"),sQuery(id+"F0.wireOp",EDGE,"E9.0.4.3"),sQuery(id+"F0.wireOp",EDGE,"E9.0.5.0"),sQuery(id+"F0.wireOp",EDGE,"E9.0.5.1"),sQuery(id+"F0.wireOp",EDGE,"E9.0.5.3"),sQuery(id+"F0.wireOp",EDGE,"E9.0.6.0"),sQuery(id+"F0.wireOp",EDGE,"E9.0.6.1"),sQuery(id+"F0.wireOp",EDGE,"E9.0.6.3"),sQuery(id+"F0.wireOp",EDGE,"E9.0.7.0"),sQuery(id+"F0.wireOp",EDGE,"E9.0.7.1"),sQuery(id+"F0.wireOp",EDGE,"E9.0.7.3"),sQuery(id+"F0.wireOp",EDGE,"E9.0.8.0"),sQuery(id+"F0.wireOp",EDGE,"E9.0.8.1"),sQuery(id+"F0.wireOp",EDGE,"E9.0.8.3"),sQuery(id+"F0.wireOp",EDGE,"E9.0.9.0"),sQuery(id+"F0.wireOp",EDGE,"E9.0.9.1"),sQuery(id+"F0.wireOp",EDGE,"E9.0.9.3"),sQuery(id+"F0.wireOp",EDGE,"E9.0.10.0"),sQuery(id+"F0.wireOp",EDGE,"E9.0.10.1"),sQuery(id+"F0.wireOp",EDGE,"E9.0.10.3"),sQuery(id+"F0.wireOp",EDGE,"E9.0.11.0"),sQuery(id+"F0.wireOp",EDGE,"E9.0.11.1"),sQuery(id+"F0.wireOp",EDGE,"E9.0.11.3"),sQuery(id+"F0.wireOp",EDGE,"E10.0.0.11"),sQuery(id+"F0.wireOp",EDGE,"E10.3.0.11"),sQuery(id+"F0.wireOp",EDGE,"E10.9.0.11")])]});
            deleteBodies(context, id + "F3", {"entities" : qUnion([Q0])});
        }
    });
